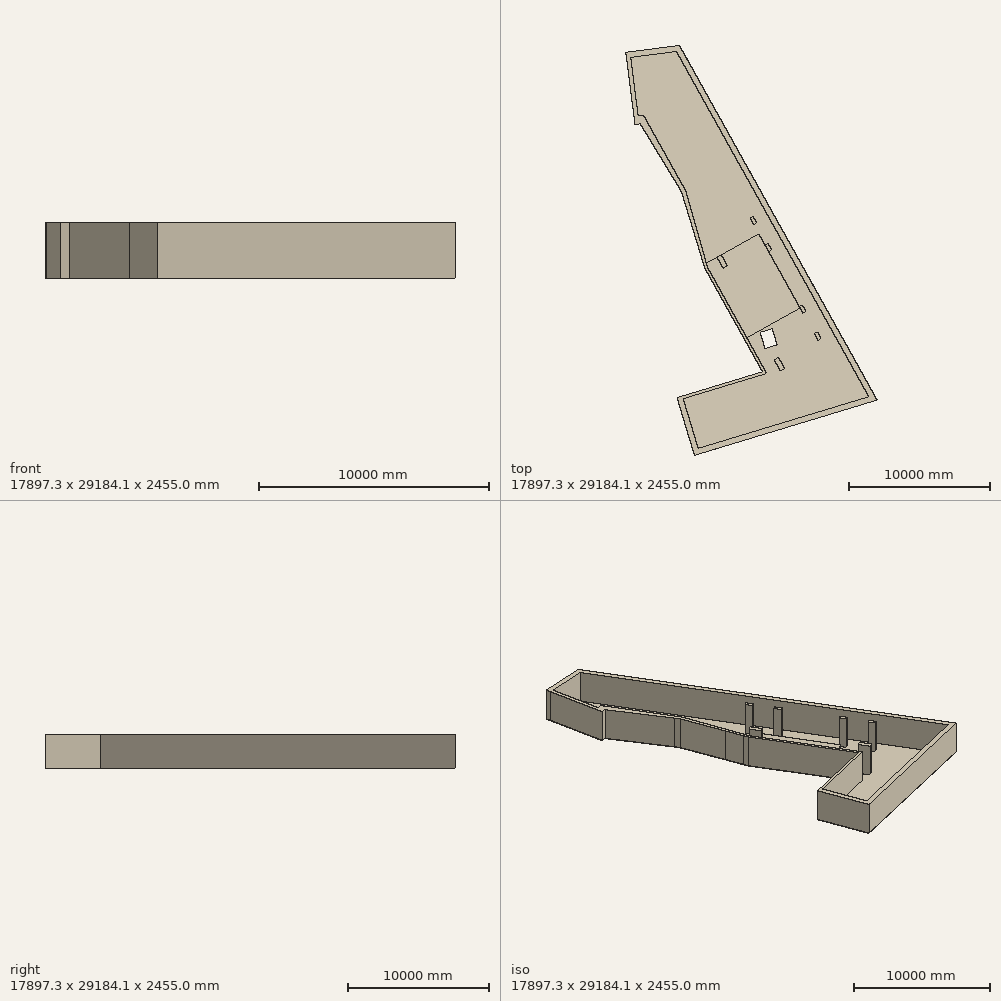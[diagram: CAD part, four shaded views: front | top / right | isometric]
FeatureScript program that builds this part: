
annotation { "Feature Type Name" : "Feature", "Feature Type Description" : "" }
export const myFeature = defineFeature(function(context is Context, id is Id, definition is map)
    precondition{}
    {
        {
            assignVariable(context, id + "F0", {"name" : "Ceiling", "anyValue" : 2430});
        }
        {
            var Q0;
            Q0=qCreatedBy(makeId("Top.planeOp"),FACE);
            var sketch = newSketch(context, id + "F1", { "sketchPlane" : qUnion([Q0])});
            skLineSegment(sketch, "E0", {"start": v(50356.24, 60225.68) * mm, "end": v(49220.2, 59881.82) * mm});
            skLineSegment(sketch, "E1", {"start": v(49220.2, 59881.82) * mm, "end": v(48658.24, 61738.46) * mm});
            skLineSegment(sketch, "E2", {"start": v(48658.24, 61738.46) * mm, "end": v(48436.53, 61671.35) * mm});
            skLineSegment(sketch, "E3", {"start": v(48436.53, 61671.35) * mm, "end": v(48364.1, 61910.63) * mm});
            skLineSegment(sketch, "E4", {"start": v(48364.1, 61910.63) * mm, "end": v(47885.55, 61765.78) * mm});
            skLineSegment(sketch, "E5", {"start": v(47885.55, 61765.78) * mm, "end": v(47957.97, 61526.5) * mm});
            skLineSegment(sketch, "E6", {"start": v(47957.97, 61526.5) * mm, "end": v(47686.86, 61444.44) * mm});
            skLineSegment(sketch, "E7", {"start": v(47686.86, 61444.44) * mm, "end": v(47759.29, 61205.16) * mm});
            skLineSegment(sketch, "E8", {"start": v(47759.29, 61205.16) * mm, "end": v(48491.38, 61426.75) * mm});
            skLineSegment(sketch, "E9", {"start": v(48491.38, 61426.75) * mm, "end": v(49070.78, 59512.52) * mm});
            skLineSegment(sketch, "E10", {"start": v(49070.78, 59512.52) * mm, "end": v(46721.47, 58801.43) * mm});
            skLineSegment(sketch, "E11", {"start": v(46721.47, 58801.43) * mm, "end": v(46142.07, 60715.66) * mm});
            skLineSegment(sketch, "E12", {"start": v(46142.07, 60715.66) * mm, "end": v(46706.46, 60886.5) * mm});
            skLineSegment(sketch, "E13", {"start": v(46706.46, 60886.5) * mm, "end": v(46634.03, 61125.77) * mm});
            skLineSegment(sketch, "E14", {"start": v(46634.03, 61125.77) * mm, "end": v(45451.68, 60767.9) * mm});
            skLineSegment(sketch, "E15", {"start": v(45451.68, 60767.9) * mm, "end": v(45524.1, 60528.62) * mm});
            skLineSegment(sketch, "E16", {"start": v(45524.1, 60528.62) * mm, "end": v(44643.85, 60262.18) * mm});
            skLineSegment(sketch, "E17", {"start": v(44643.85, 60262.18) * mm, "end": v(44571.42, 60501.46) * mm});
            skLineSegment(sketch, "E18", {"start": v(44571.42, 60501.46) * mm, "end": v(43824.87, 60275.5) * mm});
            skLineSegment(sketch, "E19", {"start": v(43824.87, 60275.5) * mm, "end": v(44386.83, 58418.88) * mm});
            skLineSegment(sketch, "E20", {"start": v(44386.83, 58418.88) * mm, "end": v(39132.43, 56828.48) * mm});
            skLineSegment(sketch, "E21", {"start": v(39132.43, 56828.48) * mm, "end": v(39132.43, 56828.48) * mm});
            skLineSegment(sketch, "E22", {"start": v(39132.43, 56828.48) * mm, "end": v(38458.91, 56624.62) * mm});
            skLineSegment(sketch, "E23", {"start": v(38458.91, 56624.62) * mm, "end": v(38574.8, 56241.77) * mm});
            skLineSegment(sketch, "E24", {"start": v(38574.8, 56241.77) * mm, "end": v(39350, 53680.63) * mm});
            skLineSegment(sketch, "E25", {"start": v(39350, 53680.63) * mm, "end": v(39348.17, 53681.01) * mm});
            skLineSegment(sketch, "E26", {"start": v(39348.17, 53681.01) * mm, "end": v(39517.02, 53123.18) * mm});
            skLineSegment(sketch, "E27", {"start": v(39517.02, 53123.18) * mm, "end": v(36984.61, 52356.67) * mm});
            skLineSegment(sketch, "E28", {"start": v(36984.61, 52356.67) * mm, "end": v(36288.15, 54657.64) * mm});
            skLineSegment(sketch, "E29", {"start": v(36288.15, 54657.64) * mm, "end": v(36288.98, 54657.9) * mm});
            skLineSegment(sketch, "E30", {"start": v(36288.98, 54657.9) * mm, "end": v(35925.26, 55857.73) * mm});
            skLineSegment(sketch, "E31", {"start": v(35925.26, 55857.73) * mm, "end": v(30957.21, 72270.12) * mm});
            skLineSegment(sketch, "E32", {"start": v(30957.21, 72270.12) * mm, "end": v(52856.55, 75078.33) * mm});
            skLineSegment(sketch, "E33", {"start": v(52856.55, 75078.33) * mm, "end": v(64538.41, 54127.57) * mm});
            skLineSegment(sketch, "E34", {"start": v(64538.41, 54127.57) * mm, "end": v(66559.72, 50502.1) * mm});
            skLineSegment(sketch, "E35", {"start": v(66559.72, 50502.1) * mm, "end": v(54412.26, 46825.31) * mm});
            skLineSegment(sketch, "E36", {"start": v(54412.26, 46825.31) * mm, "end": v(53342.81, 50358.57) * mm});
            skLineSegment(sketch, "E37", {"start": v(53342.81, 50358.57) * mm, "end": v(59288.18, 52158.11) * mm});
            skLineSegment(sketch, "E38", {"start": v(59288.18, 52158.11) * mm, "end": v(59106.76, 52483.52) * mm});
            skLineSegment(sketch, "E39", {"start": v(59106.76, 52483.52) * mm, "end": v(55867.2, 58292.84) * mm});
            skLineSegment(sketch, "E40", {"start": v(55867.2, 58292.84) * mm, "end": v(51354.69, 56926.99) * mm});
            skLineSegment(sketch, "E41", {"start": v(51354.69, 56926.99) * mm, "end": v(50356.24, 60225.68) * mm});
            skCircle(sketch, "E42", {"center": v(0, 0) * mm, "radius": 1927.6 * mm});
            skLineSegment(sketch, "E43", {"start": v(0, 5000) * mm, "end": v(0, -5000) * mm});
            skLineSegment(sketch, "E44", {"start": v(5000, 0) * mm, "end": v(-5000, 0) * mm});
            skLineSegment(sketch, "E45", {"start": v(52857.63, 75079.51) * mm, "end": v(52856.55, 75078.33) * mm});
            skLineSegment(sketch, "E46", {"start": v(52856.55, 75078.33) * mm, "end": v(56743.09, 68109.43) * mm});
            skLineSegment(sketch, "E47", {"start": v(56743.09, 68109.43) * mm, "end": v(52142.28, 67923.68) * mm});
            skLineSegment(sketch, "E48", {"start": v(52142.28, 67923.68) * mm, "end": v(32512.63, 67131.17) * mm});
            skLineSegment(sketch, "E49", {"start": v(32512.63, 67131.17) * mm, "end": v(32512.63, 67131.18) * mm});
            skLineSegment(sketch, "E50", {"start": v(32512.63, 67131.18) * mm, "end": v(30957.18, 72270.11) * mm});
            skLineSegment(sketch, "E51", {"start": v(30957.18, 72270.11) * mm, "end": v(49304.34, 74623.7) * mm});
            skLineSegment(sketch, "E52", {"start": v(49304.34, 74623.7) * mm, "end": v(49304.34, 74623.69) * mm});
            skLineSegment(sketch, "E53", {"start": v(49304.34, 74623.69) * mm, "end": v(51228.96, 74870.57) * mm});
            skLineSegment(sketch, "E54", {"start": v(51228.96, 74870.57) * mm, "end": v(52856, 75079.3) * mm});
            skLineSegment(sketch, "E55", {"start": v(44184.43, 60123.13) * mm, "end": v(45964.6, 60661.95) * mm});
            skLineSegment(sketch, "E56", {"start": v(45964.6, 60661.95) * mm, "end": v(46549.88, 58728.5) * mm});
            skLineSegment(sketch, "E57", {"start": v(46549.88, 58728.5) * mm, "end": v(44769.56, 58189.64) * mm});
            skLineSegment(sketch, "E58", {"start": v(44769.56, 58189.64) * mm, "end": v(44184.43, 60123.12) * mm});
            skLineSegment(sketch, "E59", {"start": v(44184.43, 60123.12) * mm, "end": v(44184.43, 60123.13) * mm});
            skLineSegment(sketch, "E60", {"start": v(35925.26, 55857.73) * mm, "end": v(32512.63, 67131.18) * mm});
            skLineSegment(sketch, "E61", {"start": v(32512.63, 67131.18) * mm, "end": v(56743.09, 68109.43) * mm});
            skLineSegment(sketch, "E62", {"start": v(56743.09, 68109.43) * mm, "end": v(64538.41, 54127.57) * mm});
            skLineSegment(sketch, "E63", {"start": v(53342.81, 50358.57) * mm, "end": v(51750.13, 55620.52) * mm});
            skLineSegment(sketch, "E64", {"start": v(51750.13, 55620.52) * mm, "end": v(52375.23, 55809.73) * mm});
            skLineSegment(sketch, "E65", {"start": v(52375.23, 55809.73) * mm, "end": v(53909.98, 50739.2) * mm});
            skLineSegment(sketch, "E66", {"start": v(53909.98, 50739.2) * mm, "end": v(57604, 51858.9) * mm});
            skLineSegment(sketch, "E67", {"start": v(57604, 51858.9) * mm, "end": v(55674.23, 58234.43) * mm});
            skLineSegment(sketch, "E68", {"start": v(55674.23, 58234.43) * mm, "end": v(51354.69, 56926.99) * mm});
            skLineSegment(sketch, "E69", {"start": v(51354.69, 56926.99) * mm, "end": v(55674.23, 58234.43) * mm});
            skLineSegment(sketch, "E70", {"start": v(55674.23, 58234.43) * mm, "end": v(57604.42, 51857.43) * mm});
            skLineSegment(sketch, "E71", {"start": v(57604.42, 51857.43) * mm, "end": v(53909.98, 50739.2) * mm});
            skLineSegment(sketch, "E72", {"start": v(53909.98, 50739.2) * mm, "end": v(52375.23, 55809.73) * mm});
            skLineSegment(sketch, "E73", {"start": v(52375.23, 55809.73) * mm, "end": v(51750.13, 55620.52) * mm});
            skLineSegment(sketch, "E74", {"start": v(51750.13, 55620.52) * mm, "end": v(51354.69, 56926.99) * mm});
            skLineSegment(sketch, "E75", {"start": v(43785.9, 47980.97) * mm, "end": v(41725.14, 54896.4) * mm});
            skLineSegment(sketch, "E76", {"start": v(41725.14, 54896.4) * mm, "end": v(48582.16, 57001.67) * mm});
            skLineSegment(sketch, "E77", {"start": v(48582.16, 57001.67) * mm, "end": v(50679.83, 50071.15) * mm});
            skLineSegment(sketch, "E78", {"start": v(50679.83, 50071.15) * mm, "end": v(47628.14, 49145.9) * mm});
            skLineSegment(sketch, "E79", {"start": v(47628.14, 49145.9) * mm, "end": v(47641.24, 49102.68) * mm});
            skLineSegment(sketch, "E80", {"start": v(47641.24, 49102.68) * mm, "end": v(46838.37, 48859.26) * mm});
            skLineSegment(sketch, "E81", {"start": v(46838.37, 48859.26) * mm, "end": v(46825.27, 48902.48) * mm});
            skLineSegment(sketch, "E82", {"start": v(46825.27, 48902.48) * mm, "end": v(43785.9, 47980.97) * mm});
            skLineSegment(sketch, "E83", {"start": v(43985.95, 48355.1) * mm, "end": v(50305.83, 50271.24) * mm});
            skLineSegment(sketch, "E84", {"start": v(43784.47, 47980.54) * mm, "end": v(50679.83, 50071.15) * mm});
            skLineSegment(sketch, "E85", {"start": v(42097.56, 54696.9) * mm, "end": v(43985.95, 48355.1) * mm});
            skLineSegment(sketch, "E86", {"start": v(41725.14, 54896.4) * mm, "end": v(43784.47, 47980.54) * mm});
            skLineSegment(sketch, "E87", {"start": v(48382.3, 56626.46) * mm, "end": v(42097.56, 54696.9) * mm});
            skLineSegment(sketch, "E88", {"start": v(48582.17, 57001.65) * mm, "end": v(41725.14, 54896.4) * mm});
            skLineSegment(sketch, "E89", {"start": v(50305.83, 50271.24) * mm, "end": v(48382.3, 56626.46) * mm});
            skLineSegment(sketch, "E90", {"start": v(50679.83, 50071.15) * mm, "end": v(48582.17, 57001.65) * mm});
            skLineSegment(sketch, "E91", {"start": v(57792.28, 52268.48) * mm, "end": v(58968.18, 52624.48) * mm});
            skLineSegment(sketch, "E92", {"start": v(59098.58, 52193.79) * mm, "end": v(58968.18, 52624.48) * mm});
            skLineSegment(sketch, "E93", {"start": v(57922.67, 51837.79) * mm, "end": v(59098.58, 52193.79) * mm});
            skLineSegment(sketch, "E94", {"start": v(57922.67, 51837.79) * mm, "end": v(57792.28, 52268.48) * mm});
            skLineSegment(sketch, "E95", {"start": v(61899.36, 49097.97) * mm, "end": v(50281.68, 69933.64) * mm});
            skLineSegment(sketch, "E96", {"start": v(55070.83, 59721.1) * mm, "end": v(59287.5, 52158.7) * mm});
            skLineSegment(sketch, "E97", {"start": v(54896.15, 59623.7) * mm, "end": v(58991.9, 52278.2) * mm});
            skLineSegment(sketch, "E98", {"start": v(55911.81, 59846.47) * mm, "end": v(50927.73, 58337.56) * mm});
            skLineSegment(sketch, "E99", {"start": v(51575.28, 74914.98) * mm, "end": v(49601.81, 74661.66) * mm});
            skLineSegment(sketch, "E100", {"start": v(49601.81, 74661.66) * mm, "end": v(50012.55, 71444.1) * mm});
            skLineSegment(sketch, "E101", {"start": v(50012.55, 71444.1) * mm, "end": v(62198.73, 49586.37) * mm});
            skLineSegment(sketch, "E102", {"start": v(62198.73, 49586.37) * mm, "end": v(64867.16, 51074.04) * mm});
            skLineSegment(sketch, "E103", {"start": v(64867.16, 51074.04) * mm, "end": v(51575.28, 74914.98) * mm});
            skLineSegment(sketch, "E104", {"start": v(51980.16, 57115.1) * mm, "end": v(55674.65, 58233.32) * mm});
            skLineSegment(sketch, "E105", {"start": v(55674.65, 58233.32) * mm, "end": v(57604, 51858.9) * mm});
            skLineSegment(sketch, "E106", {"start": v(57604, 51858.9) * mm, "end": v(53909.52, 50740.69) * mm});
            skLineSegment(sketch, "E107", {"start": v(53909.52, 50740.69) * mm, "end": v(51980.16, 57115.1) * mm});
            skLineSegment(sketch, "E108", {"start": v(55694.63, 56724.4) * mm, "end": v(55675.8, 56786.62) * mm});
            skLineSegment(sketch, "E109", {"start": v(55675.8, 56786.62) * mm, "end": v(55672.2, 56785.53) * mm});
            skArc(sketch, "E110", {"start": v(55672.2, 56785.53) * mm, "mid": v(55669.63, 56783.5) * mm, "end": v(55669.12, 56780.27) * mm});
            skLineSegment(sketch, "E111", {"start": v(55669.12, 56780.27) * mm, "end": v(55678.43, 56737.44) * mm});
            skArc(sketch, "E112", {"start": v(55671.21, 56725.15) * mm, "mid": v(55677.22, 56729.88) * mm, "end": v(55678.43, 56737.44) * mm});
            skLineSegment(sketch, "E113", {"start": v(55671.21, 56725.15) * mm, "end": v(55560.55, 56691.66) * mm});
            skArc(sketch, "E114", {"start": v(55547.74, 56697.88) * mm, "mid": v(55552.93, 56692.26) * mm, "end": v(55560.55, 56691.66) * mm});
            skLineSegment(sketch, "E115", {"start": v(55547.74, 56697.88) * mm, "end": v(55531.74, 56738.69) * mm});
            skArc(sketch, "E116", {"start": v(55531.74, 56738.69) * mm, "mid": v(55529.51, 56741.1) * mm, "end": v(55526.24, 56741.35) * mm});
            skLineSegment(sketch, "E117", {"start": v(55526.24, 56741.35) * mm, "end": v(55522.66, 56740.27) * mm});
            skLineSegment(sketch, "E118", {"start": v(55522.66, 56740.27) * mm, "end": v(55541.49, 56678.05) * mm});
            skLineSegment(sketch, "E119", {"start": v(55541.49, 56678.05) * mm, "end": v(55694.63, 56724.4) * mm});
            skLineSegment(sketch, "E120", {"start": v(55616.8, 56429.2) * mm, "end": v(55635.64, 56366.99) * mm});
            skLineSegment(sketch, "E121", {"start": v(55635.64, 56366.99) * mm, "end": v(55639.22, 56368.08) * mm});
            skArc(sketch, "E122", {"start": v(55639.22, 56368.08) * mm, "mid": v(55641.8, 56370.1) * mm, "end": v(55642.32, 56373.34) * mm});
            skLineSegment(sketch, "E123", {"start": v(55642.32, 56373.34) * mm, "end": v(55633, 56416.17) * mm});
            skArc(sketch, "E124", {"start": v(55640.22, 56428.45) * mm, "mid": v(55634.2, 56423.72) * mm, "end": v(55633, 56416.17) * mm});
            skLineSegment(sketch, "E125", {"start": v(55640.22, 56428.45) * mm, "end": v(55750.88, 56461.95) * mm});
            skArc(sketch, "E126", {"start": v(55763.7, 56455.73) * mm, "mid": v(55758.5, 56461.34) * mm, "end": v(55750.88, 56461.95) * mm});
            skLineSegment(sketch, "E127", {"start": v(55763.7, 56455.73) * mm, "end": v(55779.7, 56414.92) * mm});
            skArc(sketch, "E128", {"start": v(55779.7, 56414.92) * mm, "mid": v(55781.92, 56412.51) * mm, "end": v(55785.19, 56412.26) * mm});
            skLineSegment(sketch, "E129", {"start": v(55785.19, 56412.26) * mm, "end": v(55788.78, 56413.34) * mm});
            skLineSegment(sketch, "E130", {"start": v(55788.78, 56413.34) * mm, "end": v(55769.95, 56475.55) * mm});
            skLineSegment(sketch, "E131", {"start": v(55769.95, 56475.55) * mm, "end": v(55616.8, 56429.2) * mm});
            skCircle(sketch, "E132", {"center": v(55655.72, 56576.8) * mm, "radius": 0.25 * mm});
            skCircle(sketch, "E133", {"center": v(55733.93, 56318.38) * mm, "radius": 9 * mm});
            skCircle(sketch, "E134", {"center": v(55577.5, 56835.23) * mm, "radius": 9 * mm});
            skCircle(sketch, "E135", {"center": v(55405.22, 56783.08) * mm, "radius": 9 * mm});
            skCircle(sketch, "E136", {"center": v(55561.65, 56266.24) * mm, "radius": 9 * mm});
            skLineSegment(sketch, "E137", {"start": v(55367.81, 56803.1) * mm, "end": v(55654.95, 56890.01) * mm});
            skLineSegment(sketch, "E138", {"start": v(55541.63, 56228.83) * mm, "end": v(55367.81, 56803.1) * mm});
            skLineSegment(sketch, "E139", {"start": v(55828.76, 56315.74) * mm, "end": v(55541.63, 56228.83) * mm});
            skLineSegment(sketch, "E140", {"start": v(55654.95, 56890.01) * mm, "end": v(55828.76, 56315.74) * mm});
            skCircle(sketch, "E141", {"center": v(55655.72, 56576.8) * mm, "radius": 57.5 * mm});
            skCircle(sketch, "E142", {"center": v(55655.72, 56576.8) * mm, "radius": 59.5 * mm});
            skCircle(sketch, "E143", {"center": v(55655.72, 56576.8) * mm, "radius": 63.5 * mm});
            skLineSegment(sketch, "E144", {"start": v(55607.5, 56356.38) * mm, "end": v(55636.22, 56365.08) * mm});
            skLineSegment(sketch, "E145", {"start": v(55636.22, 56365.08) * mm, "end": v(55621.73, 56412.93) * mm});
            skLineSegment(sketch, "E146", {"start": v(55621.73, 56412.93) * mm, "end": v(55593.02, 56404.24) * mm});
            skLineSegment(sketch, "E147", {"start": v(55593.02, 56404.24) * mm, "end": v(55607.5, 56356.38) * mm});
            skLineSegment(sketch, "E148", {"start": v(55636.22, 56365.08) * mm, "end": v(55635.64, 56366.99) * mm});
            skLineSegment(sketch, "E149", {"start": v(55635.64, 56366.99) * mm, "end": v(55621.73, 56412.93) * mm});
            skLineSegment(sketch, "E150", {"start": v(52875.62, 55599.52) * mm, "end": v(52894.45, 55537.3) * mm});
            skLineSegment(sketch, "E151", {"start": v(52894.45, 55537.3) * mm, "end": v(52898.03, 55538.4) * mm});
            skArc(sketch, "E152", {"start": v(52898.03, 55538.4) * mm, "mid": v(52900.6, 55540.42) * mm, "end": v(52901.13, 55543.66) * mm});
            skLineSegment(sketch, "E153", {"start": v(52901.13, 55543.66) * mm, "end": v(52891.81, 55586.5) * mm});
            skArc(sketch, "E154", {"start": v(52899.03, 55598.77) * mm, "mid": v(52893.02, 55594.04) * mm, "end": v(52891.81, 55586.5) * mm});
            skLineSegment(sketch, "E155", {"start": v(52899.03, 55598.77) * mm, "end": v(53009.69, 55632.26) * mm});
            skArc(sketch, "E156", {"start": v(53022.5, 55626.05) * mm, "mid": v(53017.31, 55631.66) * mm, "end": v(53009.69, 55632.26) * mm});
            skLineSegment(sketch, "E157", {"start": v(53022.5, 55626.05) * mm, "end": v(53038.5, 55585.24) * mm});
            skArc(sketch, "E158", {"start": v(53038.5, 55585.24) * mm, "mid": v(53040.73, 55582.83) * mm, "end": v(53044, 55582.57) * mm});
            skLineSegment(sketch, "E159", {"start": v(53044, 55582.57) * mm, "end": v(53047.59, 55583.66) * mm});
            skLineSegment(sketch, "E160", {"start": v(53047.59, 55583.66) * mm, "end": v(53028.76, 55645.87) * mm});
            skLineSegment(sketch, "E161", {"start": v(53028.76, 55645.87) * mm, "end": v(52875.62, 55599.52) * mm});
            skLineSegment(sketch, "E162", {"start": v(52953.44, 55894.72) * mm, "end": v(52934.6, 55956.94) * mm});
            skLineSegment(sketch, "E163", {"start": v(52934.6, 55956.94) * mm, "end": v(52931.02, 55955.85) * mm});
            skArc(sketch, "E164", {"start": v(52931.02, 55955.85) * mm, "mid": v(52928.44, 55953.82) * mm, "end": v(52927.92, 55950.59) * mm});
            skLineSegment(sketch, "E165", {"start": v(52927.92, 55950.59) * mm, "end": v(52937.24, 55907.75) * mm});
            skArc(sketch, "E166", {"start": v(52930.02, 55895.47) * mm, "mid": v(52936.03, 55900.2) * mm, "end": v(52937.24, 55907.75) * mm});
            skLineSegment(sketch, "E167", {"start": v(52930.02, 55895.47) * mm, "end": v(52819.36, 55861.98) * mm});
            skArc(sketch, "E168", {"start": v(52806.55, 55868.2) * mm, "mid": v(52811.74, 55862.58) * mm, "end": v(52819.36, 55861.98) * mm});
            skLineSegment(sketch, "E169", {"start": v(52806.55, 55868.2) * mm, "end": v(52790.55, 55909) * mm});
            skArc(sketch, "E170", {"start": v(52790.55, 55909) * mm, "mid": v(52788.32, 55911.41) * mm, "end": v(52785.05, 55911.67) * mm});
            skLineSegment(sketch, "E171", {"start": v(52785.05, 55911.67) * mm, "end": v(52781.47, 55910.59) * mm});
            skLineSegment(sketch, "E172", {"start": v(52781.47, 55910.59) * mm, "end": v(52800.3, 55848.37) * mm});
            skLineSegment(sketch, "E173", {"start": v(52800.3, 55848.37) * mm, "end": v(52953.44, 55894.72) * mm});
            skCircle(sketch, "E174", {"center": v(52914.53, 55747.12) * mm, "radius": 0.25 * mm});
            skCircle(sketch, "E175", {"center": v(52836.3, 56005.54) * mm, "radius": 9 * mm});
            skCircle(sketch, "E176", {"center": v(52992.74, 55488.7) * mm, "radius": 9 * mm});
            skCircle(sketch, "E177", {"center": v(53165.02, 55540.84) * mm, "radius": 9 * mm});
            skCircle(sketch, "E178", {"center": v(53008.6, 56057.69) * mm, "radius": 9 * mm});
            skLineSegment(sketch, "E179", {"start": v(53202.43, 55520.82) * mm, "end": v(52915.3, 55433.91) * mm});
            skLineSegment(sketch, "E180", {"start": v(53028.61, 56095.1) * mm, "end": v(53202.43, 55520.82) * mm});
            skLineSegment(sketch, "E181", {"start": v(52741.48, 56008.19) * mm, "end": v(53028.61, 56095.1) * mm});
            skLineSegment(sketch, "E182", {"start": v(52915.3, 55433.91) * mm, "end": v(52741.48, 56008.19) * mm});
            skCircle(sketch, "E183", {"center": v(52914.53, 55747.12) * mm, "radius": 57.5 * mm});
            skCircle(sketch, "E184", {"center": v(52914.53, 55747.12) * mm, "radius": 59.5 * mm});
            skCircle(sketch, "E185", {"center": v(52914.53, 55747.12) * mm, "radius": 63.5 * mm});
            skLineSegment(sketch, "E186", {"start": v(53045.04, 55592.08) * mm, "end": v(53073.75, 55600.77) * mm});
            skLineSegment(sketch, "E187", {"start": v(53073.75, 55600.77) * mm, "end": v(53062.4, 55638.3) * mm});
            skLineSegment(sketch, "E188", {"start": v(53062.4, 55638.3) * mm, "end": v(53033.68, 55629.6) * mm});
            skLineSegment(sketch, "E189", {"start": v(53033.68, 55629.6) * mm, "end": v(53045.04, 55592.08) * mm});
            skLineSegment(sketch, "E190", {"start": v(53076.88, 55590.44) * mm, "end": v(53073.75, 55600.77) * mm});
            skLineSegment(sketch, "E191", {"start": v(53048.16, 55581.75) * mm, "end": v(53076.88, 55590.44) * mm});
            skLineSegment(sketch, "E192", {"start": v(53048.16, 55581.75) * mm, "end": v(53047.59, 55583.66) * mm});
            skLineSegment(sketch, "E193", {"start": v(53602.75, 53197.13) * mm, "end": v(53621.58, 53134.91) * mm});
            skLineSegment(sketch, "E194", {"start": v(53621.58, 53134.91) * mm, "end": v(53625.16, 53136) * mm});
            skArc(sketch, "E195", {"start": v(53625.16, 53136) * mm, "mid": v(53627.74, 53138.03) * mm, "end": v(53628.26, 53141.26) * mm});
            skLineSegment(sketch, "E196", {"start": v(53628.26, 53141.26) * mm, "end": v(53618.94, 53184.1) * mm});
            skArc(sketch, "E197", {"start": v(53626.16, 53196.38) * mm, "mid": v(53620.15, 53191.65) * mm, "end": v(53618.94, 53184.1) * mm});
            skLineSegment(sketch, "E198", {"start": v(53626.16, 53196.38) * mm, "end": v(53736.82, 53229.87) * mm});
            skArc(sketch, "E199", {"start": v(53749.63, 53223.65) * mm, "mid": v(53744.44, 53229.27) * mm, "end": v(53736.82, 53229.87) * mm});
            skLineSegment(sketch, "E200", {"start": v(53749.63, 53223.65) * mm, "end": v(53765.64, 53182.84) * mm});
            skArc(sketch, "E201", {"start": v(53765.64, 53182.84) * mm, "mid": v(53767.86, 53180.44) * mm, "end": v(53771.13, 53180.18) * mm});
            skLineSegment(sketch, "E202", {"start": v(53771.13, 53180.18) * mm, "end": v(53774.72, 53181.26) * mm});
            skLineSegment(sketch, "E203", {"start": v(53774.72, 53181.26) * mm, "end": v(53755.89, 53243.48) * mm});
            skLineSegment(sketch, "E204", {"start": v(53755.89, 53243.48) * mm, "end": v(53602.75, 53197.13) * mm});
            skLineSegment(sketch, "E205", {"start": v(53680.56, 53492.33) * mm, "end": v(53661.73, 53554.54) * mm});
            skLineSegment(sketch, "E206", {"start": v(53661.73, 53554.54) * mm, "end": v(53658.15, 53553.46) * mm});
            skArc(sketch, "E207", {"start": v(53658.15, 53553.46) * mm, "mid": v(53655.57, 53551.43) * mm, "end": v(53655.05, 53548.2) * mm});
            skLineSegment(sketch, "E208", {"start": v(53655.05, 53548.2) * mm, "end": v(53664.37, 53505.36) * mm});
            skArc(sketch, "E209", {"start": v(53657.15, 53493.08) * mm, "mid": v(53663.16, 53497.8) * mm, "end": v(53664.37, 53505.36) * mm});
            skLineSegment(sketch, "E210", {"start": v(53657.15, 53493.08) * mm, "end": v(53546.5, 53459.59) * mm});
            skArc(sketch, "E211", {"start": v(53533.68, 53465.8) * mm, "mid": v(53538.87, 53460.19) * mm, "end": v(53546.5, 53459.59) * mm});
            skLineSegment(sketch, "E212", {"start": v(53533.68, 53465.8) * mm, "end": v(53517.68, 53506.61) * mm});
            skArc(sketch, "E213", {"start": v(53517.68, 53506.61) * mm, "mid": v(53515.45, 53509.02) * mm, "end": v(53512.18, 53509.28) * mm});
            skLineSegment(sketch, "E214", {"start": v(53512.18, 53509.28) * mm, "end": v(53508.6, 53508.2) * mm});
            skLineSegment(sketch, "E215", {"start": v(53508.6, 53508.2) * mm, "end": v(53527.43, 53445.98) * mm});
            skLineSegment(sketch, "E216", {"start": v(53527.43, 53445.98) * mm, "end": v(53680.56, 53492.33) * mm});
            skCircle(sketch, "E217", {"center": v(53641.66, 53344.73) * mm, "radius": 0.25 * mm});
            skCircle(sketch, "E218", {"center": v(53563.44, 53603.15) * mm, "radius": 9 * mm});
            skCircle(sketch, "E219", {"center": v(53719.87, 53086.3) * mm, "radius": 9 * mm});
            skCircle(sketch, "E220", {"center": v(53892.15, 53138.45) * mm, "radius": 9 * mm});
            skCircle(sketch, "E221", {"center": v(53735.72, 53655.3) * mm, "radius": 9 * mm});
            skLineSegment(sketch, "E222", {"start": v(53929.56, 53118.43) * mm, "end": v(53642.42, 53031.52) * mm});
            skLineSegment(sketch, "E223", {"start": v(53755.74, 53692.7) * mm, "end": v(53929.56, 53118.43) * mm});
            skLineSegment(sketch, "E224", {"start": v(53468.6, 53605.8) * mm, "end": v(53755.74, 53692.7) * mm});
            skLineSegment(sketch, "E225", {"start": v(53642.42, 53031.52) * mm, "end": v(53468.6, 53605.8) * mm});
            skCircle(sketch, "E226", {"center": v(53641.66, 53344.73) * mm, "radius": 57.5 * mm});
            skCircle(sketch, "E227", {"center": v(53641.66, 53344.73) * mm, "radius": 59.5 * mm});
            skCircle(sketch, "E228", {"center": v(53641.66, 53344.73) * mm, "radius": 63.5 * mm});
            skLineSegment(sketch, "E229", {"start": v(53689.87, 53565.15) * mm, "end": v(53661.16, 53556.46) * mm});
            skLineSegment(sketch, "E230", {"start": v(53661.16, 53556.46) * mm, "end": v(53675.64, 53508.6) * mm});
            skLineSegment(sketch, "E231", {"start": v(53675.64, 53508.6) * mm, "end": v(53704.35, 53517.3) * mm});
            skLineSegment(sketch, "E232", {"start": v(53704.35, 53517.3) * mm, "end": v(53689.87, 53565.15) * mm});
            skLineSegment(sketch, "E233", {"start": v(53661.16, 53556.46) * mm, "end": v(53661.73, 53554.54) * mm});
            skLineSegment(sketch, "E234", {"start": v(53661.73, 53554.54) * mm, "end": v(53675.64, 53508.6) * mm});
            skLineSegment(sketch, "E235", {"start": v(56421.76, 54322) * mm, "end": v(56402.93, 54384.22) * mm});
            skLineSegment(sketch, "E236", {"start": v(56402.93, 54384.22) * mm, "end": v(56399.34, 54383.14) * mm});
            skArc(sketch, "E237", {"start": v(56399.34, 54383.14) * mm, "mid": v(56396.76, 54381.1) * mm, "end": v(56396.24, 54377.87) * mm});
            skLineSegment(sketch, "E238", {"start": v(56396.24, 54377.87) * mm, "end": v(56405.56, 54335.04) * mm});
            skArc(sketch, "E239", {"start": v(56398.34, 54322.76) * mm, "mid": v(56404.35, 54327.49) * mm, "end": v(56405.56, 54335.04) * mm});
            skLineSegment(sketch, "E240", {"start": v(56398.34, 54322.76) * mm, "end": v(56287.68, 54289.27) * mm});
            skArc(sketch, "E241", {"start": v(56274.87, 54295.48) * mm, "mid": v(56280.06, 54289.87) * mm, "end": v(56287.68, 54289.27) * mm});
            skLineSegment(sketch, "E242", {"start": v(56274.87, 54295.48) * mm, "end": v(56258.87, 54336.3) * mm});
            skArc(sketch, "E243", {"start": v(56258.87, 54336.3) * mm, "mid": v(56256.64, 54338.7) * mm, "end": v(56253.37, 54338.96) * mm});
            skLineSegment(sketch, "E244", {"start": v(56253.37, 54338.96) * mm, "end": v(56249.79, 54337.87) * mm});
            skLineSegment(sketch, "E245", {"start": v(56249.79, 54337.87) * mm, "end": v(56268.62, 54275.66) * mm});
            skLineSegment(sketch, "E246", {"start": v(56268.62, 54275.66) * mm, "end": v(56421.76, 54322) * mm});
            skLineSegment(sketch, "E247", {"start": v(56343.94, 54026.8) * mm, "end": v(56362.77, 53964.6) * mm});
            skLineSegment(sketch, "E248", {"start": v(56362.77, 53964.6) * mm, "end": v(56366.35, 53965.68) * mm});
            skArc(sketch, "E249", {"start": v(56366.35, 53965.68) * mm, "mid": v(56368.93, 53967.7) * mm, "end": v(56369.45, 53970.94) * mm});
            skLineSegment(sketch, "E250", {"start": v(56369.45, 53970.94) * mm, "end": v(56360.13, 54013.78) * mm});
            skArc(sketch, "E251", {"start": v(56367.35, 54026.06) * mm, "mid": v(56361.34, 54021.33) * mm, "end": v(56360.13, 54013.78) * mm});
            skLineSegment(sketch, "E252", {"start": v(56367.35, 54026.06) * mm, "end": v(56478, 54059.55) * mm});
            skArc(sketch, "E253", {"start": v(56490.82, 54053.33) * mm, "mid": v(56485.63, 54058.95) * mm, "end": v(56478, 54059.55) * mm});
            skLineSegment(sketch, "E254", {"start": v(56490.82, 54053.33) * mm, "end": v(56506.83, 54012.52) * mm});
            skArc(sketch, "E255", {"start": v(56506.83, 54012.52) * mm, "mid": v(56509.05, 54010.12) * mm, "end": v(56512.32, 54009.86) * mm});
            skLineSegment(sketch, "E256", {"start": v(56512.32, 54009.86) * mm, "end": v(56515.9, 54010.95) * mm});
            skLineSegment(sketch, "E257", {"start": v(56515.9, 54010.95) * mm, "end": v(56497.08, 54073.16) * mm});
            skLineSegment(sketch, "E258", {"start": v(56497.08, 54073.16) * mm, "end": v(56343.94, 54026.8) * mm});
            skCircle(sketch, "E259", {"center": v(56382.85, 54174.4) * mm, "radius": 0.25 * mm});
            skCircle(sketch, "E260", {"center": v(56461.06, 53915.99) * mm, "radius": 9 * mm});
            skCircle(sketch, "E261", {"center": v(56304.63, 54432.83) * mm, "radius": 9 * mm});
            skCircle(sketch, "E262", {"center": v(56132.35, 54380.69) * mm, "radius": 9 * mm});
            skCircle(sketch, "E263", {"center": v(56288.78, 53863.84) * mm, "radius": 9 * mm});
            skLineSegment(sketch, "E264", {"start": v(56094.94, 54400.7) * mm, "end": v(56382.08, 54487.62) * mm});
            skLineSegment(sketch, "E265", {"start": v(56268.76, 53826.44) * mm, "end": v(56094.94, 54400.7) * mm});
            skLineSegment(sketch, "E266", {"start": v(56555.9, 53913.35) * mm, "end": v(56268.76, 53826.44) * mm});
            skLineSegment(sketch, "E267", {"start": v(56382.08, 54487.62) * mm, "end": v(56555.9, 53913.35) * mm});
            skCircle(sketch, "E268", {"center": v(56382.85, 54174.4) * mm, "radius": 57.5 * mm});
            skCircle(sketch, "E269", {"center": v(56382.85, 54174.4) * mm, "radius": 59.5 * mm});
            skCircle(sketch, "E270", {"center": v(56382.85, 54174.4) * mm, "radius": 63.5 * mm});
            skLineSegment(sketch, "E271", {"start": v(56252.34, 54329.45) * mm, "end": v(56223.62, 54320.76) * mm});
            skLineSegment(sketch, "E272", {"start": v(56223.62, 54320.76) * mm, "end": v(56234.98, 54283.24) * mm});
            skLineSegment(sketch, "E273", {"start": v(56234.98, 54283.24) * mm, "end": v(56263.7, 54291.93) * mm});
            skLineSegment(sketch, "E274", {"start": v(56263.7, 54291.93) * mm, "end": v(56252.34, 54329.45) * mm});
            skLineSegment(sketch, "E275", {"start": v(56220.5, 54331.1) * mm, "end": v(56223.62, 54320.76) * mm});
            skLineSegment(sketch, "E276", {"start": v(56249.2, 54339.79) * mm, "end": v(56220.5, 54331.1) * mm});
            skLineSegment(sketch, "E277", {"start": v(56249.2, 54339.79) * mm, "end": v(56249.79, 54337.87) * mm});
            skLineSegment(sketch, "E278", {"start": v(57251.35, 51929.78) * mm, "end": v(57238.9, 51926.01) * mm});
            skLineSegment(sketch, "E279", {"start": v(57238.9, 51926.01) * mm, "end": v(57192.55, 52079.15) * mm});
            skLineSegment(sketch, "E280", {"start": v(57192.55, 52079.15) * mm, "end": v(57205, 52082.92) * mm});
            skLineSegment(sketch, "E281", {"start": v(57205, 52082.92) * mm, "end": v(57222.67, 52024.54) * mm});
            skArc(sketch, "E282", {"start": v(57222.67, 52024.54) * mm, "mid": v(57229.95, 52015.66) * mm, "end": v(57241.37, 52014.52) * mm});
            skLineSegment(sketch, "E283", {"start": v(57241.37, 52014.52) * mm, "end": v(57340.91, 52044.65) * mm});
            skArc(sketch, "E284", {"start": v(57340.91, 52044.65) * mm, "mid": v(57349.8, 52051.93) * mm, "end": v(57350.92, 52063.35) * mm});
            skLineSegment(sketch, "E285", {"start": v(57350.92, 52063.35) * mm, "end": v(57333.25, 52121.74) * mm});
            skLineSegment(sketch, "E286", {"start": v(57333.25, 52121.74) * mm, "end": v(57345.7, 52125.5) * mm});
            skLineSegment(sketch, "E287", {"start": v(57345.7, 52125.5) * mm, "end": v(57392.04, 51972.37) * mm});
            skLineSegment(sketch, "E288", {"start": v(57392.04, 51972.37) * mm, "end": v(57379.6, 51968.6) * mm});
            skLineSegment(sketch, "E289", {"start": v(57379.6, 51968.6) * mm, "end": v(57361.93, 52026.98) * mm});
            skArc(sketch, "E290", {"start": v(57361.93, 52026.98) * mm, "mid": v(57354.65, 52035.86) * mm, "end": v(57343.23, 52037) * mm});
            skLineSegment(sketch, "E291", {"start": v(57343.23, 52037) * mm, "end": v(57243.69, 52006.87) * mm});
            skArc(sketch, "E292", {"start": v(57243.69, 52006.87) * mm, "mid": v(57234.8, 51999.59) * mm, "end": v(57233.68, 51988.17) * mm});
            skLineSegment(sketch, "E293", {"start": v(57233.68, 51988.17) * mm, "end": v(57251.35, 51929.78) * mm});
            skCircle(sketch, "E294", {"center": v(57343, 51858.26) * mm, "radius": 10 * mm});
            skCircle(sketch, "E295", {"center": v(57124.8, 51975.06) * mm, "radius": 10 * mm});
            skCircle(sketch, "E296", {"center": v(57074.1, 52142.56) * mm, "radius": 10 * mm});
            skCircle(sketch, "E297", {"center": v(57175.5, 51807.57) * mm, "radius": 10 * mm});
            skCircle(sketch, "E298", {"center": v(57510.5, 51908.96) * mm, "radius": 10 * mm});
            skCircle(sketch, "E299", {"center": v(57409.1, 52243.95) * mm, "radius": 10 * mm});
            skCircle(sketch, "E300", {"center": v(57241.6, 52193.26) * mm, "radius": 10 * mm});
            skCircle(sketch, "E301", {"center": v(57459.8, 52076.46) * mm, "radius": 10 * mm});
            skLineSegment(sketch, "E302", {"start": v(57579.07, 51872.25) * mm, "end": v(57138.8, 51739) * mm});
            skLineSegment(sketch, "E303", {"start": v(57445.8, 52312.53) * mm, "end": v(57579.07, 51872.25) * mm});
            skLineSegment(sketch, "E304", {"start": v(57005.53, 52179.27) * mm, "end": v(57445.8, 52312.53) * mm});
            skLineSegment(sketch, "E305", {"start": v(57138.8, 51739) * mm, "end": v(57005.53, 52179.27) * mm});
            skLineSegment(sketch, "E306", {"start": v(54035.43, 50956.41) * mm, "end": v(54022.98, 50952.65) * mm});
            skLineSegment(sketch, "E307", {"start": v(54022.98, 50952.65) * mm, "end": v(53976.63, 51105.79) * mm});
            skLineSegment(sketch, "E308", {"start": v(53976.63, 51105.79) * mm, "end": v(53989.08, 51109.55) * mm});
            skLineSegment(sketch, "E309", {"start": v(53989.08, 51109.55) * mm, "end": v(54006.75, 51051.17) * mm});
            skArc(sketch, "E310", {"start": v(54006.75, 51051.17) * mm, "mid": v(54014.02, 51042.29) * mm, "end": v(54025.45, 51041.16) * mm});
            skLineSegment(sketch, "E311", {"start": v(54025.45, 51041.16) * mm, "end": v(54124.99, 51071.28) * mm});
            skArc(sketch, "E312", {"start": v(54124.99, 51071.28) * mm, "mid": v(54133.87, 51078.56) * mm, "end": v(54135, 51089.99) * mm});
            skLineSegment(sketch, "E313", {"start": v(54135, 51089.99) * mm, "end": v(54117.33, 51148.37) * mm});
            skLineSegment(sketch, "E314", {"start": v(54117.33, 51148.37) * mm, "end": v(54129.77, 51152.14) * mm});
            skLineSegment(sketch, "E315", {"start": v(54129.77, 51152.14) * mm, "end": v(54176.12, 50999) * mm});
            skLineSegment(sketch, "E316", {"start": v(54176.12, 50999) * mm, "end": v(54163.68, 50995.23) * mm});
            skLineSegment(sketch, "E317", {"start": v(54163.68, 50995.23) * mm, "end": v(54146, 51053.62) * mm});
            skArc(sketch, "E318", {"start": v(54146, 51053.62) * mm, "mid": v(54138.73, 51062.5) * mm, "end": v(54127.3, 51063.63) * mm});
            skLineSegment(sketch, "E319", {"start": v(54127.3, 51063.63) * mm, "end": v(54027.77, 51033.5) * mm});
            skArc(sketch, "E320", {"start": v(54027.77, 51033.5) * mm, "mid": v(54018.89, 51026.22) * mm, "end": v(54017.75, 51014.8) * mm});
            skLineSegment(sketch, "E321", {"start": v(54017.75, 51014.8) * mm, "end": v(54035.43, 50956.41) * mm});
            skCircle(sketch, "E322", {"center": v(54127.07, 50884.9) * mm, "radius": 10 * mm});
            skCircle(sketch, "E323", {"center": v(53908.88, 51001.7) * mm, "radius": 10 * mm});
            skCircle(sketch, "E324", {"center": v(53858.19, 51169.2) * mm, "radius": 10 * mm});
            skCircle(sketch, "E325", {"center": v(53959.58, 50834.2) * mm, "radius": 10 * mm});
            skCircle(sketch, "E326", {"center": v(54294.57, 50935.6) * mm, "radius": 10 * mm});
            skCircle(sketch, "E327", {"center": v(54193.18, 51270.58) * mm, "radius": 10 * mm});
            skCircle(sketch, "E328", {"center": v(54025.68, 51219.89) * mm, "radius": 10 * mm});
            skCircle(sketch, "E329", {"center": v(54243.87, 51103.09) * mm, "radius": 10 * mm});
            skLineSegment(sketch, "E330", {"start": v(54363.14, 50898.88) * mm, "end": v(53922.87, 50765.62) * mm});
            skLineSegment(sketch, "E331", {"start": v(54229.89, 51339.16) * mm, "end": v(54363.14, 50898.88) * mm});
            skLineSegment(sketch, "E332", {"start": v(53789.61, 51205.9) * mm, "end": v(54229.89, 51339.16) * mm});
            skLineSegment(sketch, "E333", {"start": v(53922.87, 50765.62) * mm, "end": v(53789.61, 51205.9) * mm});
            skLineSegment(sketch, "E334", {"start": v(52250.92, 56852.27) * mm, "end": v(52238.47, 56848.5) * mm});
            skLineSegment(sketch, "E335", {"start": v(52238.47, 56848.5) * mm, "end": v(52192.12, 57001.64) * mm});
            skLineSegment(sketch, "E336", {"start": v(52192.12, 57001.64) * mm, "end": v(52204.57, 57005.4) * mm});
            skLineSegment(sketch, "E337", {"start": v(52204.57, 57005.4) * mm, "end": v(52222.24, 56947.02) * mm});
            skArc(sketch, "E338", {"start": v(52222.24, 56947.02) * mm, "mid": v(52229.51, 56938.14) * mm, "end": v(52240.94, 56937.01) * mm});
            skLineSegment(sketch, "E339", {"start": v(52240.94, 56937.01) * mm, "end": v(52340.48, 56967.14) * mm});
            skArc(sketch, "E340", {"start": v(52340.48, 56967.14) * mm, "mid": v(52349.36, 56974.42) * mm, "end": v(52350.5, 56985.84) * mm});
            skLineSegment(sketch, "E341", {"start": v(52350.5, 56985.84) * mm, "end": v(52332.82, 57044.23) * mm});
            skLineSegment(sketch, "E342", {"start": v(52332.82, 57044.23) * mm, "end": v(52345.26, 57048) * mm});
            skLineSegment(sketch, "E343", {"start": v(52345.26, 57048) * mm, "end": v(52391.61, 56894.85) * mm});
            skLineSegment(sketch, "E344", {"start": v(52391.61, 56894.85) * mm, "end": v(52379.17, 56891.09) * mm});
            skLineSegment(sketch, "E345", {"start": v(52379.17, 56891.09) * mm, "end": v(52361.5, 56949.47) * mm});
            skArc(sketch, "E346", {"start": v(52361.5, 56949.47) * mm, "mid": v(52354.22, 56958.35) * mm, "end": v(52342.8, 56959.48) * mm});
            skLineSegment(sketch, "E347", {"start": v(52342.8, 56959.48) * mm, "end": v(52243.26, 56929.36) * mm});
            skArc(sketch, "E348", {"start": v(52243.26, 56929.36) * mm, "mid": v(52234.38, 56922.08) * mm, "end": v(52233.25, 56910.65) * mm});
            skLineSegment(sketch, "E349", {"start": v(52233.25, 56910.65) * mm, "end": v(52250.92, 56852.27) * mm});
            skCircle(sketch, "E350", {"center": v(52342.56, 56780.75) * mm, "radius": 10 * mm});
            skCircle(sketch, "E351", {"center": v(52124.37, 56897.55) * mm, "radius": 10 * mm});
            skCircle(sketch, "E352", {"center": v(52073.68, 57065.05) * mm, "radius": 10 * mm});
            skCircle(sketch, "E353", {"center": v(52175.07, 56730.06) * mm, "radius": 10 * mm});
            skCircle(sketch, "E354", {"center": v(52510.06, 56831.45) * mm, "radius": 10 * mm});
            skCircle(sketch, "E355", {"center": v(52408.67, 57166.44) * mm, "radius": 10 * mm});
            skCircle(sketch, "E356", {"center": v(52241.17, 57115.74) * mm, "radius": 10 * mm});
            skCircle(sketch, "E357", {"center": v(52459.36, 56998.94) * mm, "radius": 10 * mm});
            skLineSegment(sketch, "E358", {"start": v(52578.64, 56794.74) * mm, "end": v(52138.36, 56661.48) * mm});
            skLineSegment(sketch, "E359", {"start": v(52445.38, 57235.01) * mm, "end": v(52578.64, 56794.74) * mm});
            skLineSegment(sketch, "E360", {"start": v(52005.1, 57101.76) * mm, "end": v(52445.38, 57235.01) * mm});
            skLineSegment(sketch, "E361", {"start": v(52138.36, 56661.48) * mm, "end": v(52005.1, 57101.76) * mm});
            skLineSegment(sketch, "E362", {"start": v(55466.84, 57825.64) * mm, "end": v(55454.4, 57821.87) * mm});
            skLineSegment(sketch, "E363", {"start": v(55454.4, 57821.87) * mm, "end": v(55408.04, 57975.01) * mm});
            skLineSegment(sketch, "E364", {"start": v(55408.04, 57975.01) * mm, "end": v(55420.49, 57978.78) * mm});
            skLineSegment(sketch, "E365", {"start": v(55420.49, 57978.78) * mm, "end": v(55438.16, 57920.4) * mm});
            skArc(sketch, "E366", {"start": v(55438.16, 57920.4) * mm, "mid": v(55445.44, 57911.51) * mm, "end": v(55456.86, 57910.38) * mm});
            skLineSegment(sketch, "E367", {"start": v(55456.86, 57910.38) * mm, "end": v(55556.4, 57940.5) * mm});
            skArc(sketch, "E368", {"start": v(55556.4, 57940.5) * mm, "mid": v(55565.28, 57947.79) * mm, "end": v(55566.41, 57959.21) * mm});
            skLineSegment(sketch, "E369", {"start": v(55566.41, 57959.21) * mm, "end": v(55548.74, 58017.6) * mm});
            skLineSegment(sketch, "E370", {"start": v(55548.74, 58017.6) * mm, "end": v(55561.18, 58021.36) * mm});
            skLineSegment(sketch, "E371", {"start": v(55561.18, 58021.36) * mm, "end": v(55607.53, 57868.22) * mm});
            skLineSegment(sketch, "E372", {"start": v(55607.53, 57868.22) * mm, "end": v(55595.1, 57864.46) * mm});
            skLineSegment(sketch, "E373", {"start": v(55595.1, 57864.46) * mm, "end": v(55577.42, 57922.84) * mm});
            skArc(sketch, "E374", {"start": v(55577.42, 57922.84) * mm, "mid": v(55570.14, 57931.72) * mm, "end": v(55558.72, 57932.85) * mm});
            skLineSegment(sketch, "E375", {"start": v(55558.72, 57932.85) * mm, "end": v(55459.18, 57902.72) * mm});
            skArc(sketch, "E376", {"start": v(55459.18, 57902.72) * mm, "mid": v(55450.3, 57895.45) * mm, "end": v(55449.17, 57884.02) * mm});
            skLineSegment(sketch, "E377", {"start": v(55449.17, 57884.02) * mm, "end": v(55466.84, 57825.64) * mm});
            skCircle(sketch, "E378", {"center": v(55558.49, 57754.12) * mm, "radius": 10 * mm});
            skCircle(sketch, "E379", {"center": v(55340.3, 57870.92) * mm, "radius": 10 * mm});
            skCircle(sketch, "E380", {"center": v(55289.6, 58038.42) * mm, "radius": 10 * mm});
            skCircle(sketch, "E381", {"center": v(55391, 57703.42) * mm, "radius": 10 * mm});
            skCircle(sketch, "E382", {"center": v(55725.98, 57804.82) * mm, "radius": 10 * mm});
            skCircle(sketch, "E383", {"center": v(55624.59, 58139.8) * mm, "radius": 10 * mm});
            skCircle(sketch, "E384", {"center": v(55457.1, 58089.11) * mm, "radius": 10 * mm});
            skCircle(sketch, "E385", {"center": v(55675.29, 57972.31) * mm, "radius": 10 * mm});
            skLineSegment(sketch, "E386", {"start": v(55794.56, 57768.1) * mm, "end": v(55354.28, 57634.85) * mm});
            skLineSegment(sketch, "E387", {"start": v(55661.3, 58208.38) * mm, "end": v(55794.56, 57768.1) * mm});
            skLineSegment(sketch, "E388", {"start": v(55221.02, 58075.12) * mm, "end": v(55661.3, 58208.38) * mm});
            skLineSegment(sketch, "E389", {"start": v(55354.28, 57634.85) * mm, "end": v(55221.02, 58075.12) * mm});
            skLineSegment(sketch, "E390", {"start": v(54409.66, 51283.84) * mm, "end": v(52697.54, 56940.4) * mm});
            skLineSegment(sketch, "E391", {"start": v(52697.54, 56940.4) * mm, "end": v(55174.56, 57690.15) * mm});
            skLineSegment(sketch, "E392", {"start": v(55174.56, 57690.15) * mm, "end": v(56886.68, 52033.59) * mm});
            skLineSegment(sketch, "E393", {"start": v(56886.68, 52033.59) * mm, "end": v(54409.66, 51283.84) * mm});
            skLineSegment(sketch, "E394", {"start": v(39664.12, 55944.6) * mm, "end": v(40724.15, 52442.47) * mm});
            skLineSegment(sketch, "E395", {"start": v(38916.03, 56345.06) * mm, "end": v(39976, 52843.08) * mm});
            skLineSegment(sketch, "E396", {"start": v(40724.15, 52442.47) * mm, "end": v(36317.17, 51109.92) * mm});
            skLineSegment(sketch, "E397", {"start": v(39976, 52843.08) * mm, "end": v(36717.67, 51857.85) * mm});
            skLineSegment(sketch, "E398", {"start": v(30437.41, 72606.72) * mm, "end": v(36717.67, 51857.85) * mm});
            skLineSegment(sketch, "E399", {"start": v(29657.7, 73111.61) * mm, "end": v(36317.17, 51109.92) * mm});
            skLineSegment(sketch, "E400", {"start": v(38916.03, 56345.06) * mm, "end": v(44311.28, 57978.1) * mm});
            skLineSegment(sketch, "E401", {"start": v(44485.1, 57403.82) * mm, "end": v(44311.28, 57978.1) * mm});
            skLineSegment(sketch, "E402", {"start": v(39664.12, 55944.6) * mm, "end": v(44485.1, 57403.82) * mm});
            skLineSegment(sketch, "E403", {"start": v(29657.7, 73111.61) * mm, "end": v(53564.5, 76178.39) * mm});
            skLineSegment(sketch, "E404", {"start": v(30437.41, 72606.72) * mm, "end": v(53235.88, 75531.31) * mm});
            skLineSegment(sketch, "E405", {"start": v(68033.92, 49903.52) * mm, "end": v(54030.97, 45665.1) * mm});
            skLineSegment(sketch, "E406", {"start": v(67150.92, 50263.13) * mm, "end": v(54431.42, 46413.2) * mm});
            skLineSegment(sketch, "E407", {"start": v(54030.97, 45665.1) * mm, "end": v(49801.13, 59639.76) * mm});
            skLineSegment(sketch, "E408", {"start": v(50375.4, 59813.58) * mm, "end": v(49801.13, 59639.76) * mm});
            skLineSegment(sketch, "E409", {"start": v(54431.42, 46413.2) * mm, "end": v(50375.4, 59813.58) * mm});
            skLineSegment(sketch, "E410", {"start": v(53564.5, 76178.39) * mm, "end": v(68033.92, 49903.52) * mm});
            skLineSegment(sketch, "E411", {"start": v(53235.88, 75531.31) * mm, "end": v(67150.92, 50263.13) * mm});
            skLineSegment(sketch, "E412", {"start": v(43746.98, 61568.38) * mm, "end": v(39705.16, 60345.03) * mm});
            skLineSegment(sketch, "E413", {"start": v(39705.16, 60345.03) * mm, "end": v(39792.07, 60057.9) * mm});
            skLineSegment(sketch, "E414", {"start": v(39792.07, 60057.9) * mm, "end": v(43833.9, 61281.24) * mm});
            skLineSegment(sketch, "E415", {"start": v(43833.9, 61281.24) * mm, "end": v(43746.98, 61568.38) * mm});
            skLineSegment(sketch, "E416", {"start": v(41296.56, 69605.87) * mm, "end": v(42482.87, 61185.76) * mm});
            skLineSegment(sketch, "E417", {"start": v(48359.31, 61648.42) * mm, "end": v(47221.03, 70350.15) * mm});
            skLineSegment(sketch, "E418", {"start": v(46847.5, 70314.47) * mm, "end": v(47995.52, 61538.3) * mm});
            skLineSegment(sketch, "E419", {"start": v(55724.5, 60181.57) * mm, "end": v(50819.09, 58696.48) * mm});
            skLineSegment(sketch, "E420", {"start": v(49204.3, 59986.36) * mm, "end": v(54308.63, 61531.67) * mm});
            skLineSegment(sketch, "E421", {"start": v(48048.78, 64022.34) * mm, "end": v(52784.2, 65455.66) * mm});
            skLineSegment(sketch, "E422", {"start": v(52597.15, 65791.14) * mm, "end": v(47999.48, 64399.22) * mm});
            skLineSegment(sketch, "E423", {"start": v(54200, 61890.59) * mm, "end": v(49095.75, 60345.3) * mm});
            skLineSegment(sketch, "E424", {"start": v(32737.3, 66492.66) * mm, "end": v(35570.65, 67350.91) * mm});
            skLineSegment(sketch, "E425", {"start": v(37393.76, 61301.44) * mm, "end": v(35125.04, 68796.87) * mm});
            skLineSegment(sketch, "E426", {"start": v(37752.67, 61410.08) * mm, "end": v(35484.16, 68904.97) * mm});
            skLineSegment(sketch, "E427", {"start": v(32850.1, 66135) * mm, "end": v(35679.29, 66991.99) * mm});
            skLineSegment(sketch, "E428", {"start": v(59287.5, 52158.7) * mm, "end": v(60066.85, 52394.65) * mm});
            skLineSegment(sketch, "E429", {"start": v(57364.27, 55607.68) * mm, "end": v(58143.3, 55843.53) * mm});
            skLineSegment(sketch, "E430", {"start": v(41667.9, 69658.19) * mm, "end": v(42846.14, 61295.28) * mm});
            skLineSegment(sketch, "E431", {"start": v(37539.24, 62141.45) * mm, "end": v(41560.53, 67604.46) * mm});
            skLineSegment(sketch, "E432", {"start": v(41650.45, 67094.03) * mm, "end": v(37674.97, 61693.26) * mm});
            skLineSegment(sketch, "E433", {"start": v(31997.32, 72403.55) * mm, "end": v(33353.34, 67923.5) * mm});
            skLineSegment(sketch, "E434", {"start": v(40437.2, 70067.64) * mm, "end": v(39441.15, 73358.44) * mm});
            skLineSegment(sketch, "E435", {"start": v(33353.34, 67923.5) * mm, "end": v(40437.2, 70067.64) * mm});
            skLineSegment(sketch, "E436", {"start": v(38520.96, 69487.63) * mm, "end": v(38047.53, 73179.67) * mm});
            skLineSegment(sketch, "E437", {"start": v(38812.11, 69575.76) * mm, "end": v(38345.1, 73217.85) * mm});
            skLineSegment(sketch, "E438", {"start": v(35107.62, 70149.24) * mm, "end": v(34334.2, 72704.48) * mm});
            skLineSegment(sketch, "E439", {"start": v(34820.49, 70062.33) * mm, "end": v(34032.47, 72665.79) * mm});
            skLineSegment(sketch, "E440", {"start": v(35803.5, 68665.12) * mm, "end": v(35270.3, 72823.4) * mm});
            skLineSegment(sketch, "E441", {"start": v(36094.66, 68753.24) * mm, "end": v(35567.85, 72861.58) * mm});
            skLineSegment(sketch, "E442", {"start": v(39792.07, 60057.9) * mm, "end": v(38292.07, 59603.88) * mm});
            skLineSegment(sketch, "E443", {"start": v(39705.16, 60345.03) * mm, "end": v(38205.16, 59891.02) * mm});
            skLineSegment(sketch, "E444", {"start": v(48417.7, 61733.56) * mm, "end": v(53758.17, 63350.02) * mm});
            skLineSegment(sketch, "E445", {"start": v(48798.71, 61326.49) * mm, "end": v(53903.04, 62871.46) * mm});
            skLineSegment(sketch, "E446", {"start": v(35125.2, 68796.33) * mm, "end": v(35484.16, 68904.97) * mm});
            skLineSegment(sketch, "E447", {"start": v(37391.17, 61300.66) * mm, "end": v(37750.12, 61409.3) * mm});
            skLineSegment(sketch, "E448", {"start": v(64765.56, 53744.58) * mm, "end": v(64866.07, 53800.47) * mm});
            skLineSegment(sketch, "E449", {"start": v(64866.07, 53800.47) * mm, "end": v(65157.68, 53276.1) * mm});
            skLineSegment(sketch, "E450", {"start": v(65157.68, 53276.1) * mm, "end": v(65057.18, 53220.21) * mm});
            skLineSegment(sketch, "E451", {"start": v(65057.18, 53220.21) * mm, "end": v(64765.56, 53744.58) * mm});
            skLineSegment(sketch, "E452", {"start": v(30437.41, 72606.72) * mm, "end": v(53075.2, 75510.7) * mm});
            skLineSegment(sketch, "E453", {"start": v(30957.21, 72270.12) * mm, "end": v(52857.63, 75079.51) * mm});
            skLineSegment(sketch, "E454", {"start": v(53075.2, 75510.7) * mm, "end": v(67150.92, 50263.13) * mm});
            skLineSegment(sketch, "E455", {"start": v(52857.63, 75079.51) * mm, "end": v(66559.72, 50502.1) * mm});
            skLineSegment(sketch, "E456", {"start": v(67150.92, 50263.13) * mm, "end": v(54145.32, 46326.6) * mm});
            skLineSegment(sketch, "E457", {"start": v(66559.72, 50502.1) * mm, "end": v(54412.29, 46825.33) * mm});
            skLineSegment(sketch, "E458", {"start": v(54145.32, 46326.6) * mm, "end": v(50089.3, 59726.98) * mm});
            skLineSegment(sketch, "E459", {"start": v(54412.29, 46825.33) * mm, "end": v(50356.27, 60225.7) * mm});
            skLineSegment(sketch, "E460", {"start": v(50089.3, 59726.98) * mm, "end": v(49336.06, 59499) * mm});
            skLineSegment(sketch, "E461", {"start": v(49220.18, 59881.84) * mm, "end": v(49336.06, 59499) * mm});
            skLineSegment(sketch, "E462", {"start": v(50356.27, 60225.7) * mm, "end": v(49220.18, 59881.84) * mm});
            skLineSegment(sketch, "E463", {"start": v(39517.02, 53123.18) * mm, "end": v(38573.23, 56241.3) * mm});
            skLineSegment(sketch, "E464", {"start": v(39977.46, 52844.63) * mm, "end": v(38917.8, 56345.6) * mm});
            skLineSegment(sketch, "E465", {"start": v(35924.94, 55857.64) * mm, "end": v(44386.82, 58418.88) * mm});
            skLineSegment(sketch, "E466", {"start": v(44502.7, 58036.03) * mm, "end": v(44386.82, 58418.88) * mm});
            skLineSegment(sketch, "E467", {"start": v(38917.8, 56345.6) * mm, "end": v(44502.7, 58036.03) * mm});
            skLineSegment(sketch, "E468", {"start": v(36040.82, 55474.8) * mm, "end": v(38573.23, 56241.3) * mm});
            skLineSegment(sketch, "E469", {"start": v(30957.21, 72270.12) * mm, "end": v(36984.61, 52356.67) * mm});
            skLineSegment(sketch, "E470", {"start": v(36040.82, 55474.8) * mm, "end": v(36984.61, 52356.67) * mm});
            skLineSegment(sketch, "E471", {"start": v(30437.41, 72606.72) * mm, "end": v(36717.64, 51857.95) * mm});
            skLineSegment(sketch, "E472", {"start": v(30957.21, 72270.12) * mm, "end": v(35924.94, 55857.64) * mm});
            skLineSegment(sketch, "E473", {"start": v(36984.61, 52356.67) * mm, "end": v(39517.02, 53123.18) * mm});
            skLineSegment(sketch, "E474", {"start": v(36717.64, 51857.95) * mm, "end": v(39977.46, 52844.63) * mm});
            skCircle(sketch, "E475", {"center": v(53400.19, 75854.85) * mm, "radius": 300 * mm});
            skLineSegment(sketch, "E476", {"start": v(53400.19, 75854.85) * mm, "end": v(67780.92, 49741.01) * mm});
            skCircle(sketch, "E477", {"center": v(53759.7, 75202) * mm, "radius": 300 * mm});
            skCircle(sketch, "E478", {"center": v(54119.23, 74549.16) * mm, "radius": 300 * mm});
            skCircle(sketch, "E479", {"center": v(54478.74, 73896.31) * mm, "radius": 300 * mm});
            skCircle(sketch, "E480", {"center": v(54838.26, 73243.47) * mm, "radius": 300 * mm});
            skCircle(sketch, "E481", {"center": v(55197.78, 72590.62) * mm, "radius": 300 * mm});
            skCircle(sketch, "E482", {"center": v(55557.3, 71937.77) * mm, "radius": 300 * mm});
            skCircle(sketch, "E483", {"center": v(55916.82, 71284.93) * mm, "radius": 300 * mm});
            skCircle(sketch, "E484", {"center": v(56276.34, 70632.08) * mm, "radius": 300 * mm});
            skCircle(sketch, "E485", {"center": v(56635.85, 69979.24) * mm, "radius": 300 * mm});
            skCircle(sketch, "E486", {"center": v(56995.37, 69326.4) * mm, "radius": 300 * mm});
            skCircle(sketch, "E487", {"center": v(57354.9, 68673.55) * mm, "radius": 300 * mm});
            skCircle(sketch, "E488", {"center": v(57714.4, 68020.7) * mm, "radius": 300 * mm});
            skCircle(sketch, "E489", {"center": v(58073.93, 67367.85) * mm, "radius": 300 * mm});
            skCircle(sketch, "E490", {"center": v(58433.45, 66715) * mm, "radius": 300 * mm});
            skCircle(sketch, "E491", {"center": v(58792.97, 66062.16) * mm, "radius": 300 * mm});
            skCircle(sketch, "E492", {"center": v(59152.48, 65409.32) * mm, "radius": 300 * mm});
            skCircle(sketch, "E493", {"center": v(59512, 64756.47) * mm, "radius": 300 * mm});
            skCircle(sketch, "E494", {"center": v(59871.52, 64103.62) * mm, "radius": 300 * mm});
            skCircle(sketch, "E495", {"center": v(60231.04, 63450.78) * mm, "radius": 300 * mm});
            skCircle(sketch, "E496", {"center": v(60590.56, 62797.93) * mm, "radius": 300 * mm});
            skCircle(sketch, "E497", {"center": v(60950.08, 62145.09) * mm, "radius": 300 * mm});
            skCircle(sketch, "E498", {"center": v(61309.6, 61492.24) * mm, "radius": 300 * mm});
            skCircle(sketch, "E499", {"center": v(61669.11, 60839.4) * mm, "radius": 300 * mm});
            skCircle(sketch, "E500", {"center": v(62028.63, 60186.55) * mm, "radius": 300 * mm});
            skCircle(sketch, "E501", {"center": v(62388.15, 59533.7) * mm, "radius": 300 * mm});
            skCircle(sketch, "E502", {"center": v(62747.67, 58880.86) * mm, "radius": 300 * mm});
            skCircle(sketch, "E503", {"center": v(63107.19, 58228.01) * mm, "radius": 300 * mm});
            skCircle(sketch, "E504", {"center": v(63466.7, 57575.16) * mm, "radius": 300 * mm});
            skCircle(sketch, "E505", {"center": v(63826.22, 56922.32) * mm, "radius": 300 * mm});
            skCircle(sketch, "E506", {"center": v(64185.74, 56269.47) * mm, "radius": 300 * mm});
            skCircle(sketch, "E507", {"center": v(64545.26, 55616.63) * mm, "radius": 300 * mm});
            skCircle(sketch, "E508", {"center": v(64904.78, 54963.78) * mm, "radius": 300 * mm});
            skCircle(sketch, "E509", {"center": v(65264.3, 54310.94) * mm, "radius": 300 * mm});
            skCircle(sketch, "E510", {"center": v(65623.81, 53658.09) * mm, "radius": 300 * mm});
            skCircle(sketch, "E511", {"center": v(65983.33, 53005.24) * mm, "radius": 300 * mm});
            skCircle(sketch, "E512", {"center": v(66342.85, 52352.4) * mm, "radius": 300 * mm});
            skCircle(sketch, "E513", {"center": v(66702.37, 51699.55) * mm, "radius": 300 * mm});
            skCircle(sketch, "E514", {"center": v(67061.89, 51046.7) * mm, "radius": 300 * mm});
            skCircle(sketch, "E515", {"center": v(67421.4, 50393.86) * mm, "radius": 300 * mm});
            skCircle(sketch, "E516", {"center": v(67824.74, 49764.95) * mm, "radius": 300 * mm});
            skCircle(sketch, "E517", {"center": v(53939.47, 74875.58) * mm, "radius": 300 * mm});
            skCircle(sketch, "E518", {"center": v(54298.99, 74222.74) * mm, "radius": 300 * mm});
            skCircle(sketch, "E519", {"center": v(54658.5, 73569.89) * mm, "radius": 300 * mm});
            skCircle(sketch, "E520", {"center": v(55018.02, 72917.04) * mm, "radius": 300 * mm});
            skCircle(sketch, "E521", {"center": v(55377.54, 72264.2) * mm, "radius": 300 * mm});
            skCircle(sketch, "E522", {"center": v(55737.06, 71611.35) * mm, "radius": 300 * mm});
            skCircle(sketch, "E523", {"center": v(56096.58, 70958.5) * mm, "radius": 300 * mm});
            skCircle(sketch, "E524", {"center": v(56456.1, 70305.66) * mm, "radius": 300 * mm});
            skCircle(sketch, "E525", {"center": v(56815.61, 69652.81) * mm, "radius": 300 * mm});
            skCircle(sketch, "E526", {"center": v(57175.13, 68999.97) * mm, "radius": 300 * mm});
            skCircle(sketch, "E527", {"center": v(57534.65, 68347.12) * mm, "radius": 300 * mm});
            skCircle(sketch, "E528", {"center": v(57894.17, 67694.28) * mm, "radius": 300 * mm});
            skCircle(sketch, "E529", {"center": v(58253.69, 67041.43) * mm, "radius": 300 * mm});
            skCircle(sketch, "E530", {"center": v(58613.2, 66388.58) * mm, "radius": 300 * mm});
            skCircle(sketch, "E531", {"center": v(58972.72, 65735.74) * mm, "radius": 300 * mm});
            skCircle(sketch, "E532", {"center": v(59332.24, 65082.9) * mm, "radius": 300 * mm});
            skCircle(sketch, "E533", {"center": v(59691.76, 64430.05) * mm, "radius": 300 * mm});
            skCircle(sketch, "E534", {"center": v(60051.28, 63777.2) * mm, "radius": 300 * mm});
            skCircle(sketch, "E535", {"center": v(60410.8, 63124.35) * mm, "radius": 300 * mm});
            skCircle(sketch, "E536", {"center": v(60770.32, 62471.5) * mm, "radius": 300 * mm});
            skCircle(sketch, "E537", {"center": v(61129.83, 61818.66) * mm, "radius": 300 * mm});
            skCircle(sketch, "E538", {"center": v(61489.35, 61165.82) * mm, "radius": 300 * mm});
            skCircle(sketch, "E539", {"center": v(61848.87, 60512.97) * mm, "radius": 300 * mm});
            skCircle(sketch, "E540", {"center": v(62208.39, 59860.13) * mm, "radius": 300 * mm});
            skCircle(sketch, "E541", {"center": v(62567.9, 59207.28) * mm, "radius": 300 * mm});
            skCircle(sketch, "E542", {"center": v(62927.43, 58554.43) * mm, "radius": 300 * mm});
            skCircle(sketch, "E543", {"center": v(63286.94, 57901.59) * mm, "radius": 300 * mm});
            skCircle(sketch, "E544", {"center": v(63646.46, 57248.74) * mm, "radius": 300 * mm});
            skCircle(sketch, "E545", {"center": v(64005.98, 56595.9) * mm, "radius": 300 * mm});
            skCircle(sketch, "E546", {"center": v(64725.02, 55290.2) * mm, "radius": 300 * mm});
            skCircle(sketch, "E547", {"center": v(65084.54, 54637.36) * mm, "radius": 300 * mm});
            skCircle(sketch, "E548", {"center": v(65444.05, 53984.51) * mm, "radius": 300 * mm});
            skCircle(sketch, "E549", {"center": v(64365.5, 55943.05) * mm, "radius": 300 * mm});
            skCircle(sketch, "E550", {"center": v(65803.57, 53331.67) * mm, "radius": 300 * mm});
            skCircle(sketch, "E551", {"center": v(66163.1, 52678.82) * mm, "radius": 300 * mm});
            skCircle(sketch, "E552", {"center": v(66882.13, 51373.13) * mm, "radius": 300 * mm});
            skCircle(sketch, "E553", {"center": v(67241.65, 50720.28) * mm, "radius": 300 * mm});
            skCircle(sketch, "E554", {"center": v(66522.61, 52025.97) * mm, "radius": 300 * mm});
            skCircle(sketch, "E555", {"center": v(49888.89, 59352.88) * mm, "radius": 300 * mm});
            skCircle(sketch, "E556", {"center": v(53945.1, 45952.56) * mm, "radius": 300 * mm});
            skCircle(sketch, "E557", {"center": v(30047.42, 72859.15) * mm, "radius": 300 * mm});
            skCircle(sketch, "E558", {"center": v(33293.56, 62134.5) * mm, "radius": 300 * mm});
            skCircle(sketch, "E559", {"center": v(33077.15, 62849.46) * mm, "radius": 300 * mm});
            skCircle(sketch, "E560", {"center": v(32860.74, 63564.43) * mm, "radius": 300 * mm});
            skCircle(sketch, "E561", {"center": v(32644.34, 64279.4) * mm, "radius": 300 * mm});
            skCircle(sketch, "E562", {"center": v(32427.93, 64994.36) * mm, "radius": 300 * mm});
            skCircle(sketch, "E563", {"center": v(32211.53, 65709.33) * mm, "radius": 300 * mm});
            skCircle(sketch, "E564", {"center": v(31995.12, 66424.3) * mm, "radius": 300 * mm});
            skCircle(sketch, "E565", {"center": v(31778.71, 67139.26) * mm, "radius": 300 * mm});
            skCircle(sketch, "E566", {"center": v(31562.3, 67854.23) * mm, "radius": 300 * mm});
            skCircle(sketch, "E567", {"center": v(31345.9, 68569.2) * mm, "radius": 300 * mm});
            skCircle(sketch, "E568", {"center": v(31129.5, 69284.16) * mm, "radius": 300 * mm});
            skCircle(sketch, "E569", {"center": v(30913.1, 69999.13) * mm, "radius": 300 * mm});
            skCircle(sketch, "E570", {"center": v(30696.68, 70714.1) * mm, "radius": 300 * mm});
            skCircle(sketch, "E571", {"center": v(30480.28, 71429.06) * mm, "radius": 300 * mm});
            skCircle(sketch, "E572", {"center": v(30263.87, 72144.03) * mm, "radius": 300 * mm});
            skCircle(sketch, "E573", {"center": v(30777.44, 72952.8) * mm, "radius": 300 * mm});
            skCircle(sketch, "E574", {"center": v(31507.46, 73046.44) * mm, "radius": 300 * mm});
            skCircle(sketch, "E575", {"center": v(32237.47, 73140.09) * mm, "radius": 300 * mm});
            skCircle(sketch, "E576", {"center": v(32967.5, 73233.74) * mm, "radius": 300 * mm});
            skCircle(sketch, "E577", {"center": v(33697.51, 73327.38) * mm, "radius": 300 * mm});
            skCircle(sketch, "E578", {"center": v(34427.53, 73421.03) * mm, "radius": 300 * mm});
            skCircle(sketch, "E579", {"center": v(35157.55, 73514.68) * mm, "radius": 300 * mm});
            skCircle(sketch, "E580", {"center": v(35887.56, 73608.32) * mm, "radius": 300 * mm});
            skCircle(sketch, "E581", {"center": v(36617.58, 73701.97) * mm, "radius": 300 * mm});
            skCircle(sketch, "E582", {"center": v(37347.6, 73795.62) * mm, "radius": 300 * mm});
            skCircle(sketch, "E583", {"center": v(38077.62, 73889.27) * mm, "radius": 300 * mm});
            skCircle(sketch, "E584", {"center": v(38807.64, 73982.91) * mm, "radius": 300 * mm});
            skCircle(sketch, "E585", {"center": v(39537.65, 74076.56) * mm, "radius": 300 * mm});
            skCircle(sketch, "E586", {"center": v(40267.67, 74170.2) * mm, "radius": 300 * mm});
            skCircle(sketch, "E587", {"center": v(40997.7, 74263.85) * mm, "radius": 300 * mm});
            skCircle(sketch, "E588", {"center": v(41727.7, 74357.5) * mm, "radius": 300 * mm});
            skCircle(sketch, "E589", {"center": v(42457.73, 74451.15) * mm, "radius": 300 * mm});
            skCircle(sketch, "E590", {"center": v(43187.74, 74544.8) * mm, "radius": 300 * mm});
            skCircle(sketch, "E591", {"center": v(43917.76, 74638.44) * mm, "radius": 300 * mm});
            skCircle(sketch, "E592", {"center": v(44647.78, 74732.09) * mm, "radius": 300 * mm});
            skCircle(sketch, "E593", {"center": v(45377.8, 74825.74) * mm, "radius": 300 * mm});
            skCircle(sketch, "E594", {"center": v(46107.82, 74919.38) * mm, "radius": 300 * mm});
            skCircle(sketch, "E595", {"center": v(46837.83, 75013.03) * mm, "radius": 300 * mm});
            skCircle(sketch, "E596", {"center": v(47567.85, 75106.68) * mm, "radius": 300 * mm});
            skCircle(sketch, "E597", {"center": v(48297.87, 75200.32) * mm, "radius": 300 * mm});
            skCircle(sketch, "E598", {"center": v(49027.89, 75293.97) * mm, "radius": 300 * mm});
            skCircle(sketch, "E599", {"center": v(49757.9, 75387.62) * mm, "radius": 300 * mm});
            skCircle(sketch, "E600", {"center": v(50487.92, 75481.26) * mm, "radius": 300 * mm});
            skCircle(sketch, "E601", {"center": v(51217.94, 75574.91) * mm, "radius": 300 * mm});
            skCircle(sketch, "E602", {"center": v(51947.96, 75668.56) * mm, "radius": 300 * mm});
            skCircle(sketch, "E603", {"center": v(52677.98, 75762.2) * mm, "radius": 300 * mm});
            skCircle(sketch, "E604", {"center": v(54664.85, 46170.41) * mm, "radius": 300 * mm});
            skCircle(sketch, "E605", {"center": v(55384.6, 46388.28) * mm, "radius": 300 * mm});
            skCircle(sketch, "E606", {"center": v(56104.35, 46606.14) * mm, "radius": 300 * mm});
            skCircle(sketch, "E607", {"center": v(56824.1, 46824) * mm, "radius": 300 * mm});
            skCircle(sketch, "E608", {"center": v(57543.85, 47041.87) * mm, "radius": 300 * mm});
            skCircle(sketch, "E609", {"center": v(58263.6, 47259.73) * mm, "radius": 300 * mm});
            skCircle(sketch, "E610", {"center": v(58983.35, 47477.6) * mm, "radius": 300 * mm});
            skCircle(sketch, "E611", {"center": v(59703.1, 47695.46) * mm, "radius": 300 * mm});
            skCircle(sketch, "E612", {"center": v(60422.84, 47913.33) * mm, "radius": 300 * mm});
            skCircle(sketch, "E613", {"center": v(61142.6, 48131.2) * mm, "radius": 300 * mm});
            skCircle(sketch, "E614", {"center": v(61862.34, 48349.06) * mm, "radius": 300 * mm});
            skCircle(sketch, "E615", {"center": v(62582.1, 48566.92) * mm, "radius": 300 * mm});
            skCircle(sketch, "E616", {"center": v(63301.84, 48784.78) * mm, "radius": 300 * mm});
            skCircle(sketch, "E617", {"center": v(64021.6, 49002.65) * mm, "radius": 300 * mm});
            skCircle(sketch, "E618", {"center": v(64741.34, 49220.51) * mm, "radius": 300 * mm});
            skCircle(sketch, "E619", {"center": v(65461.09, 49438.38) * mm, "radius": 300 * mm});
            skCircle(sketch, "E620", {"center": v(66180.84, 49656.24) * mm, "radius": 300 * mm});
            skCircle(sketch, "E621", {"center": v(53731.58, 46657.95) * mm, "radius": 300 * mm});
            skCircle(sketch, "E622", {"center": v(53518.06, 47363.34) * mm, "radius": 300 * mm});
            skCircle(sketch, "E623", {"center": v(53304.54, 48068.73) * mm, "radius": 300 * mm});
            skCircle(sketch, "E624", {"center": v(53091.02, 48774.13) * mm, "radius": 300 * mm});
            skCircle(sketch, "E625", {"center": v(52877.5, 49479.52) * mm, "radius": 300 * mm});
            skCircle(sketch, "E626", {"center": v(52663.99, 50184.91) * mm, "radius": 300 * mm});
            skCircle(sketch, "E627", {"center": v(52450.47, 50890.3) * mm, "radius": 300 * mm});
            skCircle(sketch, "E628", {"center": v(52236.95, 51595.7) * mm, "radius": 300 * mm});
            skCircle(sketch, "E629", {"center": v(52023.43, 52301.1) * mm, "radius": 300 * mm});
            skCircle(sketch, "E630", {"center": v(51809.91, 53006.48) * mm, "radius": 300 * mm});
            skCircle(sketch, "E631", {"center": v(51596.4, 53711.88) * mm, "radius": 300 * mm});
            skCircle(sketch, "E632", {"center": v(51382.87, 54417.27) * mm, "radius": 300 * mm});
            skCircle(sketch, "E633", {"center": v(51169.35, 55122.66) * mm, "radius": 300 * mm});
            skCircle(sketch, "E634", {"center": v(50955.84, 55828.05) * mm, "radius": 300 * mm});
            skCircle(sketch, "E635", {"center": v(50742.32, 56533.45) * mm, "radius": 300 * mm});
            skCircle(sketch, "E636", {"center": v(50528.8, 57238.84) * mm, "radius": 300 * mm});
            skCircle(sketch, "E637", {"center": v(50315.28, 57944.23) * mm, "radius": 300 * mm});
            skCircle(sketch, "E638", {"center": v(50101.76, 58649.62) * mm, "radius": 300 * mm});
            skLineSegment(sketch, "E639", {"start": v(30047.42, 72859.15) * mm, "end": v(35457.62, 54984.83) * mm});
            skLineSegment(sketch, "E640", {"start": v(53945.1, 45952.56) * mm, "end": v(49888.89, 59352.88) * mm});
            skLineSegment(sketch, "E641", {"start": v(53945.1, 45952.56) * mm, "end": v(66900.59, 49874.1) * mm});
            skLineSegment(sketch, "E642", {"start": v(30047.42, 72859.15) * mm, "end": v(53400.19, 75854.85) * mm});
            skCircle(sketch, "E643", {"center": v(53579.95, 75528.43) * mm, "radius": 300 * mm});
            skCircle(sketch, "E644", {"center": v(40161.14, 53266.98) * mm, "radius": 300 * mm});
            skCircle(sketch, "E645", {"center": v(39509.32, 55420.5) * mm, "radius": 300 * mm});
            skCircle(sketch, "E646", {"center": v(39726.6, 54702.66) * mm, "radius": 300 * mm});
            skCircle(sketch, "E647", {"center": v(39943.87, 53984.82) * mm, "radius": 300 * mm});
            skCircle(sketch, "E648", {"center": v(44086.3, 57596.56) * mm, "radius": 300 * mm});
            skCircle(sketch, "E649", {"center": v(42647.96, 57161.2) * mm, "radius": 300 * mm});
            skCircle(sketch, "E650", {"center": v(43367, 57378.84) * mm, "radius": 300 * mm});
            skCircle(sketch, "E651", {"center": v(33483.8, 61505.57) * mm, "radius": 300 * mm});
            skLineSegment(sketch, "E652", {"start": v(40350.08, 52642.78) * mm, "end": v(39290.08, 56144.84) * mm});
            skLineSegment(sketch, "E653", {"start": v(36517.3, 51483.84) * mm, "end": v(35457.62, 54984.83) * mm});
            skCircle(sketch, "E654", {"center": v(33621.22, 60726.77) * mm, "radius": 375 * mm});
            skLineSegment(sketch, "E655", {"start": v(35123.8, 56106.32) * mm, "end": v(35600.08, 54499.8) * mm});
            skLineSegment(sketch, "E656", {"start": v(34931.23, 56052.24) * mm, "end": v(35408.33, 54442.95) * mm});
            skLineSegment(sketch, "E657", {"start": v(34713.87, 57650.93) * mm, "end": v(35123.8, 56106.32) * mm});
            skLineSegment(sketch, "E658", {"start": v(34522.07, 57593.97) * mm, "end": v(34931.23, 56052.24) * mm});
            skLineSegment(sketch, "E659", {"start": v(34069.7, 59608.22) * mm, "end": v(34713.87, 57650.93) * mm});
            skLineSegment(sketch, "E660", {"start": v(33879.73, 59545.7) * mm, "end": v(34522.07, 57593.97) * mm});
            skLineSegment(sketch, "E661", {"start": v(33879.73, 59545.7) * mm, "end": v(34069.7, 59608.22) * mm});
            skCircle(sketch, "E662", {"center": v(35503.23, 54471.13) * mm, "radius": 375 * mm});
            skCircle(sketch, "E663", {"center": v(35024.65, 56078.4) * mm, "radius": 375 * mm});
            skCircle(sketch, "E664", {"center": v(34617.97, 57622.45) * mm, "radius": 300 * mm});
            skCircle(sketch, "E665", {"center": v(33974.72, 59576.96) * mm, "radius": 375 * mm});
            skCircle(sketch, "E666", {"center": v(35948.4, 52971.91) * mm, "radius": 375 * mm});
            skCircle(sketch, "E667", {"center": v(36387.31, 51517) * mm, "radius": 375 * mm});
            skCircle(sketch, "E668", {"center": v(37796.6, 51792.76) * mm, "radius": 375 * mm});
            skCircle(sketch, "E669", {"center": v(39835.27, 56332.54) * mm, "radius": 375 * mm});
            skCircle(sketch, "E670", {"center": v(41846.6, 56950.07) * mm, "radius": 375 * mm});
            skLineSegment(sketch, "E671", {"start": v(35706.21, 54140.42) * mm, "end": v(35937.9, 53360.17) * mm});
            skLineSegment(sketch, "E672", {"start": v(35746.17, 53303.24) * mm, "end": v(35937.9, 53360.17) * mm});
            skLineSegment(sketch, "E673", {"start": v(35514.49, 54083.49) * mm, "end": v(35746.17, 53303.24) * mm});
            skLineSegment(sketch, "E674", {"start": v(35514.49, 54083.49) * mm, "end": v(35706.21, 54140.42) * mm});
            skLineSegment(sketch, "E675", {"start": v(36152.82, 52642.08) * mm, "end": v(36375.12, 51905.21) * mm});
            skLineSegment(sketch, "E676", {"start": v(36183.64, 51847.45) * mm, "end": v(36375.12, 51905.21) * mm});
            skLineSegment(sketch, "E677", {"start": v(35961.34, 52584.32) * mm, "end": v(36183.64, 51847.45) * mm});
            skLineSegment(sketch, "E678", {"start": v(35961.34, 52584.32) * mm, "end": v(36152.82, 52642.08) * mm});
            skLineSegment(sketch, "E679", {"start": v(36736.53, 51687.4) * mm, "end": v(37409.39, 51818.95) * mm});
            skLineSegment(sketch, "E680", {"start": v(37447.76, 51622.67) * mm, "end": v(37409.39, 51818.95) * mm});
            skLineSegment(sketch, "E681", {"start": v(36774.9, 51491.12) * mm, "end": v(37447.76, 51622.67) * mm});
            skLineSegment(sketch, "E682", {"start": v(36774.9, 51491.12) * mm, "end": v(36736.53, 51687.4) * mm});
            skLineSegment(sketch, "E683", {"start": v(40164.4, 56538.2) * mm, "end": v(41458.77, 56935.6) * mm});
            skLineSegment(sketch, "E684", {"start": v(41517.47, 56744.4) * mm, "end": v(41458.77, 56935.6) * mm});
            skLineSegment(sketch, "E685", {"start": v(40223.1, 56347) * mm, "end": v(41517.47, 56744.4) * mm});
            skLineSegment(sketch, "E686", {"start": v(40223.1, 56347) * mm, "end": v(40164.4, 56538.2) * mm});
            skCircle(sketch, "E687", {"center": v(38530.81, 52093.36) * mm, "radius": 300 * mm});
            skCircle(sketch, "E688", {"center": v(39248.7, 52310.48) * mm, "radius": 300 * mm});
            skCircle(sketch, "E689", {"center": v(39966.5, 52527.84) * mm, "radius": 300 * mm});
            skLineSegment(sketch, "E690", {"start": v(36517.4, 51483.94) * mm, "end": v(40348.6, 52643.57) * mm});
            skLineSegment(sketch, "E691", {"start": v(39290.08, 56144.84) * mm, "end": v(44398.2, 57690.92) * mm});
            skCircle(sketch, "E692", {"center": v(67171.9, 49625.85) * mm, "radius": 300 * mm});
            skLineSegment(sketch, "E693", {"start": v(43459.74, 61481.43) * mm, "end": v(43746.88, 61568.34) * mm});
            skLineSegment(sketch, "E694", {"start": v(43746.88, 61568.34) * mm, "end": v(43833.79, 61281.2) * mm});
            skLineSegment(sketch, "E695", {"start": v(43833.79, 61281.2) * mm, "end": v(43546.65, 61194.3) * mm});
            skLineSegment(sketch, "E696", {"start": v(43546.65, 61194.3) * mm, "end": v(43459.74, 61481.43) * mm});
            skLineSegment(sketch, "E697", {"start": v(43546.65, 61194.3) * mm, "end": v(43824.77, 60275.46) * mm});
            skLineSegment(sketch, "E698", {"start": v(43833.79, 61281.2) * mm, "end": v(44112, 60362.4) * mm});
            skLineSegment(sketch, "E699", {"start": v(49601.8, 74661.76) * mm, "end": v(50131.26, 70514.15) * mm});
            skLineSegment(sketch, "E700", {"start": v(49304.21, 74623.77) * mm, "end": v(49909.66, 69880.9) * mm});
            skLineSegment(sketch, "E701", {"start": v(49304.21, 74623.77) * mm, "end": v(49601.8, 74661.76) * mm});
            skLineSegment(sketch, "E702", {"start": v(47015.81, 71647.18) * mm, "end": v(47180.44, 70357.55) * mm});
            skLineSegment(sketch, "E703", {"start": v(46882.85, 70319.56) * mm, "end": v(47180.44, 70357.55) * mm});
            skLineSegment(sketch, "E704", {"start": v(46718.23, 71609.2) * mm, "end": v(46882.85, 70319.56) * mm});
            skLineSegment(sketch, "E705", {"start": v(46718.23, 71609.2) * mm, "end": v(47015.81, 71647.18) * mm});
            skLineSegment(sketch, "E706", {"start": v(41460.6, 70937.97) * mm, "end": v(41625.98, 69648.52) * mm});
            skLineSegment(sketch, "E707", {"start": v(41328.42, 69610.36) * mm, "end": v(41625.98, 69648.52) * mm});
            skLineSegment(sketch, "E708", {"start": v(41163.04, 70899.8) * mm, "end": v(41328.42, 69610.36) * mm});
            skLineSegment(sketch, "E709", {"start": v(41163.04, 70899.8) * mm, "end": v(41460.6, 70937.97) * mm});
            skLineSegment(sketch, "E710", {"start": v(38209.1, 59892.17) * mm, "end": v(43746.98, 61568.38) * mm});
            skLineSegment(sketch, "E711", {"start": v(42856.08, 61298.72) * mm, "end": v(43746.98, 61568.38) * mm});
            skLineSegment(sketch, "E712", {"start": v(38296.02, 59605.04) * mm, "end": v(43833.9, 61281.24) * mm});
            skLineSegment(sketch, "E713", {"start": v(38209.1, 59892.17) * mm, "end": v(42377.52, 61153.87) * mm});
            skLineSegment(sketch, "E714", {"start": v(37749.93, 61409.25) * mm, "end": v(39136.07, 56829.58) * mm});
            skLineSegment(sketch, "E715", {"start": v(38296.02, 59605.04) * mm, "end": v(39136.07, 56829.58) * mm});
            skLineSegment(sketch, "E716", {"start": v(37462.8, 61322.34) * mm, "end": v(38848.93, 56742.67) * mm});
            skLineSegment(sketch, "E717", {"start": v(37749.93, 61409.25) * mm, "end": v(38209.1, 59892.17) * mm});
            skLineSegment(sketch, "E718", {"start": v(56060.35, 60596.37) * mm, "end": v(56498.65, 59810.3) * mm});
            skLineSegment(sketch, "E719", {"start": v(56192.96, 59639.86) * mm, "end": v(56498.65, 59810.3) * mm});
            skLineSegment(sketch, "E720", {"start": v(55754.66, 60425.92) * mm, "end": v(56192.96, 59639.86) * mm});
            skLineSegment(sketch, "E721", {"start": v(55754.66, 60425.92) * mm, "end": v(56060.35, 60596.37) * mm});
            skLineSegment(sketch, "E722", {"start": v(43746.88, 61568.34) * mm, "end": v(43459.74, 61481.43) * mm});
            skLineSegment(sketch, "E723", {"start": v(43833.79, 61281.2) * mm, "end": v(43746.88, 61568.34) * mm});
            skLineSegment(sketch, "E724", {"start": v(44643.83, 60262.21) * mm, "end": v(44184.42, 60123.16) * mm});
            skLineSegment(sketch, "E725", {"start": v(44571.41, 60501.5) * mm, "end": v(43824.87, 60275.54) * mm});
            skLineSegment(sketch, "E726", {"start": v(46706.45, 60886.5) * mm, "end": v(45505.24, 60522.94) * mm});
            skLineSegment(sketch, "E727", {"start": v(46634.03, 61125.79) * mm, "end": v(45432.82, 60762.22) * mm});
            skLineSegment(sketch, "E728", {"start": v(48505.84, 61431.13) * mm, "end": v(47759.29, 61205.17) * mm});
            skLineSegment(sketch, "E729", {"start": v(48672.7, 61742.83) * mm, "end": v(47686.86, 61444.45) * mm});
            skLineSegment(sketch, "E730", {"start": v(45469.03, 60642.58) * mm, "end": v(45505.24, 60522.94) * mm});
            skLineSegment(sketch, "E731", {"start": v(44607.62, 60381.85) * mm, "end": v(44643.83, 60262.21) * mm});
            skLineSegment(sketch, "E732", {"start": v(45469.03, 60642.58) * mm, "end": v(45432.82, 60762.22) * mm});
            skLineSegment(sketch, "E733", {"start": v(44607.62, 60381.85) * mm, "end": v(44571.41, 60501.5) * mm});
            skLineSegment(sketch, "E734", {"start": v(44571.41, 60501.5) * mm, "end": v(45432.82, 60762.22) * mm});
            skLineSegment(sketch, "E735", {"start": v(44643.83, 60262.21) * mm, "end": v(45505.24, 60522.94) * mm});
            skLineSegment(sketch, "E736", {"start": v(47723.07, 61324.8) * mm, "end": v(47759.29, 61205.17) * mm});
            skLineSegment(sketch, "E737", {"start": v(46670.24, 61006.15) * mm, "end": v(46706.45, 60886.5) * mm});
            skLineSegment(sketch, "E738", {"start": v(47723.07, 61324.8) * mm, "end": v(47686.86, 61444.45) * mm});
            skLineSegment(sketch, "E739", {"start": v(46670.24, 61006.15) * mm, "end": v(46634.03, 61125.79) * mm});
            skLineSegment(sketch, "E740", {"start": v(46634.03, 61125.79) * mm, "end": v(47686.86, 61444.45) * mm});
            skLineSegment(sketch, "E741", {"start": v(46706.45, 60886.5) * mm, "end": v(47759.29, 61205.17) * mm});
            skLineSegment(sketch, "E742", {"start": v(48672.7, 61742.83) * mm, "end": v(49476.62, 59086.75) * mm});
            skLineSegment(sketch, "E743", {"start": v(48505.84, 61431.13) * mm, "end": v(49091.04, 59497.67) * mm});
            skLineSegment(sketch, "E744", {"start": v(44184.42, 60123.16) * mm, "end": v(44769.56, 58189.64) * mm});
            skLineSegment(sketch, "E745", {"start": v(43824.87, 60275.54) * mm, "end": v(44628.7, 57619.38) * mm});
            skLineSegment(sketch, "E746", {"start": v(46549.88, 58728.5) * mm, "end": v(45964.7, 60661.96) * mm});
            skLineSegment(sketch, "E747", {"start": v(46741.3, 58786.45) * mm, "end": v(46156.12, 60719.9) * mm});
            skLineSegment(sketch, "E748", {"start": v(49726, 58953.22) * mm, "end": v(44495.31, 57370.09) * mm});
            skLineSegment(sketch, "E749", {"start": v(49476.63, 59086.71) * mm, "end": v(44628.8, 57619.45) * mm});
            skLineSegment(sketch, "E750", {"start": v(49476.62, 59086.75) * mm, "end": v(44628.7, 57619.38) * mm});
            skLineSegment(sketch, "E751", {"start": v(49091.04, 59497.67) * mm, "end": v(46741.3, 58786.45) * mm});
            skLineSegment(sketch, "E752", {"start": v(44495.31, 57370.09) * mm, "end": v(44311.28, 57978.1) * mm});
            skLineSegment(sketch, "E753", {"start": v(44502.7, 58036.03) * mm, "end": v(44311.28, 57978.1) * mm});
            skLineSegment(sketch, "E754", {"start": v(44628.8, 57619.45) * mm, "end": v(44502.7, 58036.03) * mm});
            skLineSegment(sketch, "E755", {"start": v(60131.76, 53293.71) * mm, "end": v(60570.05, 52507.65) * mm});
            skLineSegment(sketch, "E756", {"start": v(60264.36, 52337.2) * mm, "end": v(60570.05, 52507.65) * mm});
            skLineSegment(sketch, "E757", {"start": v(59826.06, 53123.27) * mm, "end": v(60264.36, 52337.2) * mm});
            skLineSegment(sketch, "E758", {"start": v(59826.06, 53123.27) * mm, "end": v(60131.76, 53293.71) * mm});
            skLineSegment(sketch, "E759", {"start": v(47885.55, 61765.78) * mm, "end": v(48364.1, 61910.63) * mm});
            skLineSegment(sketch, "E760", {"start": v(47957.97, 61526.5) * mm, "end": v(48436.53, 61671.35) * mm});
            skLineSegment(sketch, "E761", {"start": v(47957.97, 61526.5) * mm, "end": v(47885.55, 61765.78) * mm});
            skLineSegment(sketch, "E762", {"start": v(34583.64, 74073.32) * mm, "end": v(34277.71, 74103.31) * mm});
            skLineSegment(sketch, "E763", {"start": v(36509.2, 74336.72) * mm, "end": v(36210.42, 74264.44) * mm});
            skLineSegment(sketch, "E764", {"start": v(38568.06, 74568.37) * mm, "end": v(38260.66, 74568.37) * mm});
            skLineSegment(sketch, "E765", {"start": v(40630.85, 74832.8) * mm, "end": v(40326.88, 74787.02) * mm});
            skLineSegment(sketch, "E766", {"start": v(42529.89, 75035.76) * mm, "end": v(42224.21, 75003.22) * mm});
            skLineSegment(sketch, "E767", {"start": v(44620.7, 75346.4) * mm, "end": v(44315.83, 75306.98) * mm});
            skLineSegment(sketch, "E768", {"start": v(46260.89, 75467.94) * mm, "end": v(45954.04, 75449.5) * mm});
            skLineSegment(sketch, "E769", {"start": v(48411.94, 75732.02) * mm, "end": v(48106.56, 75696.83) * mm});
            skLineSegment(sketch, "E770", {"start": v(34308.4, 74416.31) * mm, "end": v(34614.33, 74386.32) * mm});
            skLineSegment(sketch, "E771", {"start": v(34306.57, 74397.7) * mm, "end": v(34612.5, 74367.7) * mm});
            skLineSegment(sketch, "E772", {"start": v(34614.33, 74386.32) * mm, "end": v(34612.5, 74367.7) * mm});
            skLineSegment(sketch, "E773", {"start": v(34585.47, 74091.93) * mm, "end": v(34583.64, 74073.32) * mm});
            skLineSegment(sketch, "E774", {"start": v(34585.47, 74091.93) * mm, "end": v(34279.53, 74121.92) * mm});
            skLineSegment(sketch, "E775", {"start": v(34277.71, 74103.31) * mm, "end": v(34279.53, 74121.92) * mm});
            skLineSegment(sketch, "E776", {"start": v(34306.57, 74397.7) * mm, "end": v(34308.4, 74416.31) * mm});
            skLineSegment(sketch, "E777", {"start": v(34465.5, 74382.12) * mm, "end": v(34438.47, 74106.34) * mm});
            skLineSegment(sketch, "E778", {"start": v(34453.57, 74383.29) * mm, "end": v(34426.53, 74107.51) * mm});
            skLineSegment(sketch, "E779", {"start": v(36136.47, 74570.12) * mm, "end": v(36435.25, 74642.4) * mm});
            skLineSegment(sketch, "E780", {"start": v(36140.87, 74551.95) * mm, "end": v(36439.65, 74624.22) * mm});
            skLineSegment(sketch, "E781", {"start": v(36435.25, 74642.4) * mm, "end": v(36439.65, 74624.22) * mm});
            skLineSegment(sketch, "E782", {"start": v(36504.8, 74354.9) * mm, "end": v(36509.2, 74336.72) * mm});
            skLineSegment(sketch, "E783", {"start": v(36504.8, 74354.9) * mm, "end": v(36206.02, 74282.62) * mm});
            skLineSegment(sketch, "E784", {"start": v(36210.42, 74264.44) * mm, "end": v(36206.02, 74282.62) * mm});
            skLineSegment(sketch, "E785", {"start": v(36140.87, 74551.95) * mm, "end": v(36136.47, 74570.12) * mm});
            skLineSegment(sketch, "E786", {"start": v(36296.1, 74589.5) * mm, "end": v(36361.24, 74320.16) * mm});
            skLineSegment(sketch, "E787", {"start": v(36284.43, 74586.68) * mm, "end": v(36349.58, 74317.34) * mm});
            skLineSegment(sketch, "E788", {"start": v(38260.66, 74882.87) * mm, "end": v(38568.06, 74882.87) * mm});
            skLineSegment(sketch, "E789", {"start": v(38260.66, 74864.17) * mm, "end": v(38568.06, 74864.17) * mm});
            skLineSegment(sketch, "E790", {"start": v(38568.06, 74882.87) * mm, "end": v(38568.06, 74864.17) * mm});
            skLineSegment(sketch, "E791", {"start": v(38568.06, 74587.07) * mm, "end": v(38568.06, 74568.37) * mm});
            skLineSegment(sketch, "E792", {"start": v(38568.06, 74587.07) * mm, "end": v(38260.66, 74587.07) * mm});
            skLineSegment(sketch, "E793", {"start": v(38260.66, 74568.37) * mm, "end": v(38260.66, 74587.07) * mm});
            skLineSegment(sketch, "E794", {"start": v(38260.66, 74864.17) * mm, "end": v(38260.66, 74882.87) * mm});
            skLineSegment(sketch, "E795", {"start": v(38420.36, 74864.17) * mm, "end": v(38420.36, 74587.07) * mm});
            skLineSegment(sketch, "E796", {"start": v(38408.36, 74864.17) * mm, "end": v(38408.36, 74587.07) * mm});
            skLineSegment(sketch, "E797", {"start": v(40280.05, 75098.01) * mm, "end": v(40584.02, 75143.79) * mm});
            skLineSegment(sketch, "E798", {"start": v(40282.83, 75079.52) * mm, "end": v(40586.8, 75125.3) * mm});
            skLineSegment(sketch, "E799", {"start": v(40584.02, 75143.79) * mm, "end": v(40586.8, 75125.3) * mm});
            skLineSegment(sketch, "E800", {"start": v(40628.07, 74851.29) * mm, "end": v(40630.85, 74832.8) * mm});
            skLineSegment(sketch, "E801", {"start": v(40628.07, 74851.29) * mm, "end": v(40324.1, 74805.5) * mm});
            skLineSegment(sketch, "E802", {"start": v(40326.88, 74787.02) * mm, "end": v(40324.1, 74805.5) * mm});
            skLineSegment(sketch, "E803", {"start": v(40282.83, 75079.52) * mm, "end": v(40280.05, 75098.01) * mm});
            skLineSegment(sketch, "E804", {"start": v(40440.75, 75103.3) * mm, "end": v(40482.02, 74829.3) * mm});
            skLineSegment(sketch, "E805", {"start": v(40428.89, 75101.51) * mm, "end": v(40470.15, 74827.5) * mm});
            skLineSegment(sketch, "E806", {"start": v(42190.92, 75315.95) * mm, "end": v(42496.6, 75348.5) * mm});
            skLineSegment(sketch, "E807", {"start": v(42192.9, 75297.36) * mm, "end": v(42498.58, 75329.9) * mm});
            skLineSegment(sketch, "E808", {"start": v(42496.6, 75348.5) * mm, "end": v(42498.58, 75329.9) * mm});
            skLineSegment(sketch, "E809", {"start": v(42527.9, 75054.35) * mm, "end": v(42529.89, 75035.76) * mm});
            skLineSegment(sketch, "E810", {"start": v(42527.9, 75054.35) * mm, "end": v(42222.24, 75021.82) * mm});
            skLineSegment(sketch, "E811", {"start": v(42224.21, 75003.22) * mm, "end": v(42222.24, 75021.82) * mm});
            skLineSegment(sketch, "E812", {"start": v(42192.9, 75297.36) * mm, "end": v(42190.92, 75315.95) * mm});
            skLineSegment(sketch, "E813", {"start": v(42351.7, 75314.26) * mm, "end": v(42381.04, 75038.72) * mm});
            skLineSegment(sketch, "E814", {"start": v(42339.77, 75313) * mm, "end": v(42369.1, 75037.45) * mm});
            skLineSegment(sketch, "E815", {"start": v(44275.5, 75618.88) * mm, "end": v(44580.37, 75658.3) * mm});
            skLineSegment(sketch, "E816", {"start": v(44277.9, 75600.34) * mm, "end": v(44582.77, 75639.76) * mm});
            skLineSegment(sketch, "E817", {"start": v(44580.37, 75658.3) * mm, "end": v(44582.77, 75639.76) * mm});
            skLineSegment(sketch, "E818", {"start": v(44618.3, 75364.94) * mm, "end": v(44620.7, 75346.4) * mm});
            skLineSegment(sketch, "E819", {"start": v(44618.3, 75364.94) * mm, "end": v(44313.44, 75325.53) * mm});
            skLineSegment(sketch, "E820", {"start": v(44315.83, 75306.98) * mm, "end": v(44313.44, 75325.53) * mm});
            skLineSegment(sketch, "E821", {"start": v(44277.9, 75600.34) * mm, "end": v(44275.5, 75618.88) * mm});
            skLineSegment(sketch, "E822", {"start": v(44436.28, 75620.82) * mm, "end": v(44471.82, 75346) * mm});
            skLineSegment(sketch, "E823", {"start": v(44424.38, 75619.28) * mm, "end": v(44459.92, 75344.46) * mm});
            skLineSegment(sketch, "E824", {"start": v(45935.18, 75763.44) * mm, "end": v(46242.02, 75781.88) * mm});
            skLineSegment(sketch, "E825", {"start": v(45936.3, 75744.77) * mm, "end": v(46243.14, 75763.21) * mm});
            skLineSegment(sketch, "E826", {"start": v(46242.02, 75781.88) * mm, "end": v(46243.14, 75763.21) * mm});
            skLineSegment(sketch, "E827", {"start": v(46259.76, 75486.61) * mm, "end": v(46260.89, 75467.94) * mm});
            skLineSegment(sketch, "E828", {"start": v(46259.76, 75486.61) * mm, "end": v(45952.92, 75468.17) * mm});
            skLineSegment(sketch, "E829", {"start": v(45954.04, 75449.5) * mm, "end": v(45952.92, 75468.17) * mm});
            skLineSegment(sketch, "E830", {"start": v(45936.3, 75744.77) * mm, "end": v(45935.18, 75763.44) * mm});
            skLineSegment(sketch, "E831", {"start": v(46095.71, 75754.35) * mm, "end": v(46112.33, 75477.75) * mm});
            skLineSegment(sketch, "E832", {"start": v(46083.73, 75753.63) * mm, "end": v(46100.35, 75477.03) * mm});
            skLineSegment(sketch, "E833", {"start": v(48070.56, 76009.27) * mm, "end": v(48375.94, 76044.45) * mm});
            skLineSegment(sketch, "E834", {"start": v(48072.7, 75990.69) * mm, "end": v(48378.08, 76025.87) * mm});
            skLineSegment(sketch, "E835", {"start": v(48375.94, 76044.45) * mm, "end": v(48378.08, 76025.87) * mm});
            skLineSegment(sketch, "E836", {"start": v(48409.8, 75750.6) * mm, "end": v(48411.94, 75732.02) * mm});
            skLineSegment(sketch, "E837", {"start": v(48409.8, 75750.6) * mm, "end": v(48104.42, 75715.4) * mm});
            skLineSegment(sketch, "E838", {"start": v(48106.56, 75696.83) * mm, "end": v(48104.42, 75715.4) * mm});
            skLineSegment(sketch, "E839", {"start": v(48072.7, 75990.69) * mm, "end": v(48070.56, 76009.27) * mm});
            skLineSegment(sketch, "E840", {"start": v(48231.35, 76008.97) * mm, "end": v(48263.07, 75733.69) * mm});
            skLineSegment(sketch, "E841", {"start": v(48219.43, 76007.6) * mm, "end": v(48251.15, 75732.31) * mm});
            skLineSegment(sketch, "E842", {"start": v(34452, 74244.23) * mm, "end": v(34440.05, 74245.4) * mm});
            skLineSegment(sketch, "E843", {"start": v(36328.67, 74454.83) * mm, "end": v(36317, 74452) * mm});
            skLineSegment(sketch, "E844", {"start": v(38420.36, 74725.62) * mm, "end": v(38408.36, 74725.62) * mm});
            skLineSegment(sketch, "E845", {"start": v(40461.39, 74966.3) * mm, "end": v(40449.52, 74964.5) * mm});
            skLineSegment(sketch, "E846", {"start": v(42366.37, 75176.5) * mm, "end": v(42354.44, 75175.22) * mm});
            skLineSegment(sketch, "E847", {"start": v(44454.05, 75483.4) * mm, "end": v(44442.15, 75481.87) * mm});
            skLineSegment(sketch, "E848", {"start": v(46104.02, 75616.05) * mm, "end": v(46092.04, 75615.33) * mm});
            skLineSegment(sketch, "E849", {"start": v(48247.21, 75871.33) * mm, "end": v(48235.3, 75869.95) * mm});
            skCircle(sketch, "E850", {"center": v(34446.02, 74244.82) * mm, "radius": 300 * mm});
            skCircle(sketch, "E851", {"center": v(36322.84, 74453.42) * mm, "radius": 300 * mm});
            skCircle(sketch, "E852", {"center": v(38414.36, 74725.62) * mm, "radius": 300 * mm});
            skCircle(sketch, "E853", {"center": v(40455.45, 74965.4) * mm, "radius": 300 * mm});
            skCircle(sketch, "E854", {"center": v(42360.4, 75175.86) * mm, "radius": 300 * mm});
            skCircle(sketch, "E855", {"center": v(44448.1, 75482.64) * mm, "radius": 300 * mm});
            skCircle(sketch, "E856", {"center": v(46098.03, 75615.7) * mm, "radius": 300 * mm});
            skCircle(sketch, "E857", {"center": v(48241.25, 75870.64) * mm, "radius": 300 * mm});
            skCircle(sketch, "E858", {"center": v(34776.7, 58413.82) * mm, "radius": 328.69 * mm});
            skCircle(sketch, "E859", {"center": v(35224.5, 57091.4) * mm, "radius": 323.11 * mm});
            skCircle(sketch, "E860", {"center": v(35826.9, 55480) * mm, "radius": 308.82 * mm});
            skCircle(sketch, "E861", {"center": v(36309.94, 53902.1) * mm, "radius": 312.62 * mm});
            skCircle(sketch, "E862", {"center": v(36823.57, 52431.1) * mm, "radius": 314.17 * mm});
            skCircle(sketch, "E863", {"center": v(37258.05, 50987.66) * mm, "radius": 280.53 * mm});
            skLineSegment(sketch, "E864", {"start": v(44215.6, 60106.43) * mm, "end": v(45947.99, 60630.79) * mm});
            skLineSegment(sketch, "E865", {"start": v(45947.99, 60630.79) * mm, "end": v(46469.45, 58907.97) * mm});
            skLineSegment(sketch, "E866", {"start": v(46469.45, 58907.97) * mm, "end": v(44737.06, 58383.62) * mm});
            skLineSegment(sketch, "E867", {"start": v(44737.06, 58383.62) * mm, "end": v(44215.6, 60106.43) * mm});
            skLineSegment(sketch, "E868", {"start": v(44643.85, 60262.18) * mm, "end": v(45505.25, 60522.9) * mm});
            skLineSegment(sketch, "E869", {"start": v(49476.63, 59086.71) * mm, "end": v(49350.51, 59503.37) * mm});
            skLineSegment(sketch, "E870", {"start": v(49726, 58953.22) * mm, "end": v(49541.94, 59561.3) * mm});
            skLineSegment(sketch, "E871", {"start": v(51278.99, 57177.09) * mm, "end": v(56516.32, 58762.32) * mm});
            skLineSegment(sketch, "E872", {"start": v(56665.85, 58494.14) * mm, "end": v(51365.9, 56889.95) * mm});
            skLineSegment(sketch, "E873", {"start": v(50131.26, 70514.15) * mm, "end": v(50593.39, 70573.29) * mm});
            skLineSegment(sketch, "E874", {"start": v(50669.54, 69978.14) * mm, "end": v(50593.39, 70573.29) * mm});
            skLineSegment(sketch, "E875", {"start": v(49909.66, 69880.9) * mm, "end": v(50669.54, 69978.14) * mm});
            skLineSegment(sketch, "E876", {"start": v(47841.4, 61911.65) * mm, "end": v(48319.95, 62056.5) * mm});
            skLineSegment(sketch, "E877", {"start": v(48392.38, 61817.22) * mm, "end": v(48319.95, 62056.5) * mm});
            skLineSegment(sketch, "E878", {"start": v(47913.82, 61672.37) * mm, "end": v(48392.38, 61817.22) * mm});
            skLineSegment(sketch, "E879", {"start": v(47913.82, 61672.37) * mm, "end": v(47841.4, 61911.65) * mm});
            skLineSegment(sketch, "E880", {"start": v(58318.92, 63332.61) * mm, "end": v(58586.76, 62852.24) * mm});
            skLineSegment(sketch, "E881", {"start": v(58368.41, 62730.5) * mm, "end": v(58586.76, 62852.24) * mm});
            skLineSegment(sketch, "E882", {"start": v(58100.57, 63210.86) * mm, "end": v(58368.41, 62730.5) * mm});
            skLineSegment(sketch, "E883", {"start": v(58100.57, 63210.86) * mm, "end": v(58318.92, 63332.61) * mm});
            skLineSegment(sketch, "E884", {"start": v(59393.32, 61405.46) * mm, "end": v(59661.17, 60925.09) * mm});
            skLineSegment(sketch, "E885", {"start": v(59442.82, 60803.34) * mm, "end": v(59661.17, 60925.09) * mm});
            skLineSegment(sketch, "E886", {"start": v(59174.97, 61283.7) * mm, "end": v(59442.82, 60803.34) * mm});
            skLineSegment(sketch, "E887", {"start": v(59174.97, 61283.7) * mm, "end": v(59393.32, 61405.46) * mm});
            skLineSegment(sketch, "E888", {"start": v(61824.92, 57043.9) * mm, "end": v(62092.77, 56563.53) * mm});
            skLineSegment(sketch, "E889", {"start": v(61874.42, 56441.78) * mm, "end": v(62092.77, 56563.53) * mm});
            skLineSegment(sketch, "E890", {"start": v(61606.57, 56922.15) * mm, "end": v(61874.42, 56441.78) * mm});
            skLineSegment(sketch, "E891", {"start": v(61606.57, 56922.15) * mm, "end": v(61824.92, 57043.9) * mm});
            skLineSegment(sketch, "E892", {"start": v(62899.33, 55116.74) * mm, "end": v(63167.18, 54636.37) * mm});
            skLineSegment(sketch, "E893", {"start": v(62948.82, 54514.62) * mm, "end": v(63167.18, 54636.37) * mm});
            skLineSegment(sketch, "E894", {"start": v(62680.98, 54995) * mm, "end": v(62948.82, 54514.62) * mm});
            skLineSegment(sketch, "E895", {"start": v(62680.98, 54995) * mm, "end": v(62899.33, 55116.74) * mm});
            skLineSegment(sketch, "E896", {"start": v(55887.31, 67694.17) * mm, "end": v(56155.16, 67213.8) * mm});
            skLineSegment(sketch, "E897", {"start": v(55936.81, 67092.05) * mm, "end": v(56155.16, 67213.8) * mm});
            skLineSegment(sketch, "E898", {"start": v(55668.96, 67572.42) * mm, "end": v(55936.81, 67092.05) * mm});
            skLineSegment(sketch, "E899", {"start": v(55668.96, 67572.42) * mm, "end": v(55887.31, 67694.17) * mm});
            skLineSegment(sketch, "E900", {"start": v(54812.9, 69621.33) * mm, "end": v(55080.76, 69140.96) * mm});
            skLineSegment(sketch, "E901", {"start": v(54862.4, 69019.2) * mm, "end": v(55080.76, 69140.96) * mm});
            skLineSegment(sketch, "E902", {"start": v(54594.56, 69499.58) * mm, "end": v(54862.4, 69019.2) * mm});
            skLineSegment(sketch, "E903", {"start": v(54594.56, 69499.58) * mm, "end": v(54812.9, 69621.33) * mm});
            skLineSegment(sketch, "E904", {"start": v(56155.16, 67213.8) * mm, "end": v(55936.81, 67092.05) * mm});
            skLineSegment(sketch, "E905", {"start": v(55936.81, 67092.05) * mm, "end": v(55668.96, 67572.42) * mm});
            skLineSegment(sketch, "E906", {"start": v(57613.6, 55160.75) * mm, "end": v(58392.95, 55396.7) * mm});
            skLineSegment(sketch, "E907", {"start": v(59038.3, 52605.67) * mm, "end": v(59817.63, 52841.6) * mm});
            skLineSegment(sketch, "E908", {"start": v(52375.25, 73993.75) * mm, "end": v(52643.1, 73513.38) * mm});
            skLineSegment(sketch, "E909", {"start": v(52424.75, 73391.63) * mm, "end": v(52643.1, 73513.38) * mm});
            skLineSegment(sketch, "E910", {"start": v(52156.9, 73872) * mm, "end": v(52424.75, 73391.63) * mm});
            skLineSegment(sketch, "E911", {"start": v(52156.9, 73872) * mm, "end": v(52375.25, 73993.75) * mm});
            skLineSegment(sketch, "E912", {"start": v(52281.23, 65747.36) * mm, "end": v(53057.73, 65982.39) * mm});
            skLineSegment(sketch, "E913", {"start": v(52418.84, 65292.73) * mm, "end": v(53000.6, 65468.81) * mm});
            skLineSegment(sketch, "E914", {"start": v(52418.84, 65292.73) * mm, "end": v(52281.23, 65747.36) * mm});
            skLineSegment(sketch, "E915", {"start": v(54045.3, 63436.93) * mm, "end": v(55287.74, 59332.08) * mm});
            skLineSegment(sketch, "E916", {"start": v(53758.17, 63350.02) * mm, "end": v(54874.02, 59663.37) * mm});
            skLineSegment(sketch, "E917", {"start": v(53380.3, 65116.29) * mm, "end": v(53523.86, 65159.74) * mm});
            skLineSegment(sketch, "E918", {"start": v(53901.74, 63393.47) * mm, "end": v(54045.3, 63436.93) * mm});
            skLineSegment(sketch, "E919", {"start": v(53380.3, 65116.29) * mm, "end": v(53236.72, 65072.83) * mm});
            skLineSegment(sketch, "E920", {"start": v(53901.74, 63393.47) * mm, "end": v(53758.17, 63350.02) * mm});
            skLineSegment(sketch, "E921", {"start": v(53758.17, 63350.02) * mm, "end": v(53236.72, 65072.83) * mm});
            skLineSegment(sketch, "E922", {"start": v(54045.3, 63436.93) * mm, "end": v(53523.86, 65159.74) * mm});
            skLineSegment(sketch, "E923", {"start": v(53236.72, 65072.83) * mm, "end": v(53758.17, 63350.02) * mm});
            skLineSegment(sketch, "E924", {"start": v(53523.86, 65159.74) * mm, "end": v(54045.3, 63436.93) * mm});
            skLineSegment(sketch, "E925", {"start": v(35194.47, 68817.29) * mm, "end": v(34817.9, 70061.55) * mm});
            skLineSegment(sketch, "E926", {"start": v(35105.03, 70148.46) * mm, "end": v(34817.9, 70061.55) * mm});
            skLineSegment(sketch, "E927", {"start": v(35481.6, 68904.2) * mm, "end": v(35105.03, 70148.46) * mm});
            skLineSegment(sketch, "E928", {"start": v(35481.6, 68904.2) * mm, "end": v(35194.47, 68817.29) * mm});
            skLineSegment(sketch, "E929", {"start": v(42377.52, 61153.87) * mm, "end": v(42261.62, 61536.8) * mm});
            skLineSegment(sketch, "E930", {"start": v(42740.18, 61681.65) * mm, "end": v(42261.62, 61536.8) * mm});
            skLineSegment(sketch, "E931", {"start": v(42856.08, 61298.72) * mm, "end": v(42740.18, 61681.65) * mm});
            skLineSegment(sketch, "E932", {"start": v(53225.02, 65066.3) * mm, "end": v(53000.6, 65468.81) * mm});
            skLineSegment(sketch, "E933", {"start": v(53487.04, 65212.4) * mm, "end": v(53057.73, 65982.39) * mm});
            skLineSegment(sketch, "E934", {"start": v(59287.5, 52158.7) * mm, "end": v(53342.63, 50359.31) * mm});
            skLineSegment(sketch, "E935", {"start": v(58991.9, 52278.2) * mm, "end": v(53284.69, 50550.73) * mm});
            skLineSegment(sketch, "E936", {"start": v(58991.9, 52278.2) * mm, "end": v(59187.82, 52337.5) * mm});
            skLineSegment(sketch, "E937", {"start": v(55287.74, 59332.08) * mm, "end": v(59187.82, 52337.5) * mm});
            skLineSegment(sketch, "E938", {"start": v(54874.02, 59663.37) * mm, "end": v(58991.9, 52278.2) * mm});
            skLineSegment(sketch, "E939", {"start": v(61463.3, 49888.88) * mm, "end": v(61702.18, 49961.19) * mm});
            skLineSegment(sketch, "E940", {"start": v(61702.18, 49961.19) * mm, "end": v(61774.6, 49721.9) * mm});
            skLineSegment(sketch, "E941", {"start": v(61774.6, 49721.9) * mm, "end": v(61535.73, 49649.6) * mm});
            skLineSegment(sketch, "E942", {"start": v(61535.73, 49649.6) * mm, "end": v(61463.3, 49888.88) * mm});
            skLineSegment(sketch, "E943", {"start": v(53291.1, 65935.67) * mm, "end": v(53529.97, 66007.97) * mm});
            skLineSegment(sketch, "E944", {"start": v(53529.97, 66007.97) * mm, "end": v(53602.4, 65768.7) * mm});
            skLineSegment(sketch, "E945", {"start": v(53602.4, 65768.7) * mm, "end": v(53363.52, 65696.4) * mm});
            skLineSegment(sketch, "E946", {"start": v(53363.52, 65696.4) * mm, "end": v(53291.1, 65935.67) * mm});
            skLineSegment(sketch, "E947", {"start": v(65900.3, 51172.38) * mm, "end": v(66118.29, 51293.9) * mm});
            skLineSegment(sketch, "E948", {"start": v(66118.29, 51293.9) * mm, "end": v(66240.02, 51075.55) * mm});
            skLineSegment(sketch, "E949", {"start": v(66240.02, 51075.55) * mm, "end": v(66022.03, 50954.02) * mm});
            skLineSegment(sketch, "E950", {"start": v(66022.03, 50954.02) * mm, "end": v(65900.3, 51172.38) * mm});
            skLineSegment(sketch, "E951", {"start": v(43166.65, 61878.55) * mm, "end": v(43405.52, 61950.85) * mm});
            skLineSegment(sketch, "E952", {"start": v(43405.52, 61950.85) * mm, "end": v(43477.94, 61711.57) * mm});
            skLineSegment(sketch, "E953", {"start": v(43477.94, 61711.57) * mm, "end": v(43239.07, 61639.27) * mm});
            skLineSegment(sketch, "E954", {"start": v(43239.07, 61639.27) * mm, "end": v(43166.65, 61878.55) * mm});
            skLineSegment(sketch, "E955", {"start": v(48366.02, 61911.21) * mm, "end": v(48604.9, 61983.51) * mm});
            skLineSegment(sketch, "E956", {"start": v(48604.9, 61983.51) * mm, "end": v(48677.32, 61744.23) * mm});
            skLineSegment(sketch, "E957", {"start": v(48677.32, 61744.23) * mm, "end": v(48438.45, 61671.93) * mm});
            skLineSegment(sketch, "E958", {"start": v(48438.45, 61671.93) * mm, "end": v(48366.02, 61911.21) * mm});
            skLineSegment(sketch, "E959", {"start": v(64065.34, 54464.23) * mm, "end": v(64283.47, 54585.5) * mm});
            skLineSegment(sketch, "E960", {"start": v(64283.47, 54585.5) * mm, "end": v(64404.95, 54367) * mm});
            skLineSegment(sketch, "E961", {"start": v(64404.95, 54367) * mm, "end": v(64186.82, 54245.73) * mm});
            skLineSegment(sketch, "E962", {"start": v(64186.82, 54245.73) * mm, "end": v(64065.34, 54464.23) * mm});
            skLineSegment(sketch, "E963", {"start": v(45953.73, 61181.06) * mm, "end": v(46192.6, 61253.36) * mm});
            skLineSegment(sketch, "E964", {"start": v(46192.6, 61253.36) * mm, "end": v(46265.03, 61014.08) * mm});
            skLineSegment(sketch, "E965", {"start": v(46265.03, 61014.08) * mm, "end": v(46026.16, 60941.78) * mm});
            skLineSegment(sketch, "E966", {"start": v(46026.16, 60941.78) * mm, "end": v(45953.73, 61181.06) * mm});
            skLineSegment(sketch, "E967", {"start": v(52418.02, 67337.58) * mm, "end": v(52656.9, 67409.89) * mm});
            skLineSegment(sketch, "E968", {"start": v(52656.9, 67409.89) * mm, "end": v(52729.32, 67170.6) * mm});
            skLineSegment(sketch, "E969", {"start": v(52729.32, 67170.6) * mm, "end": v(52490.45, 67098.3) * mm});
            skLineSegment(sketch, "E970", {"start": v(52490.45, 67098.3) * mm, "end": v(52418.02, 67337.58) * mm});
            skLineSegment(sketch, "E971", {"start": v(4.94, 5000) * mm, "end": v(0, -5000) * mm});
            skLineSegment(sketch, "E972", {"start": v(5000, 0) * mm, "end": v(-5000, -4.94) * mm});
            skCircle(sketch, "E973", {"center": v(0, -2.47) * mm, "radius": 1929.43 * mm});
            skLineSegment(sketch, "E974", {"start": v(58325.52, 53471.87) * mm, "end": v(58500.2, 53569.27) * mm});
            skLineSegment(sketch, "E975", {"start": v(58500.2, 53569.27) * mm, "end": v(58889.8, 52870.55) * mm});
            skLineSegment(sketch, "E976", {"start": v(58889.8, 52870.55) * mm, "end": v(58715.12, 52773.15) * mm});
            skLineSegment(sketch, "E977", {"start": v(58715.12, 52773.15) * mm, "end": v(58325.52, 53471.87) * mm});
            skLineSegment(sketch, "E978", {"start": v(32883.91, 66080.85) * mm, "end": v(33122.79, 66153.15) * mm});
            skLineSegment(sketch, "E979", {"start": v(33122.79, 66153.15) * mm, "end": v(33195.21, 65913.87) * mm});
            skLineSegment(sketch, "E980", {"start": v(33195.21, 65913.87) * mm, "end": v(32956.34, 65841.57) * mm});
            skLineSegment(sketch, "E981", {"start": v(32956.34, 65841.57) * mm, "end": v(32883.91, 66080.85) * mm});
            skLineSegment(sketch, "E982", {"start": v(32882.84, 66524.7) * mm, "end": v(32930.7, 66539.19) * mm});
            skLineSegment(sketch, "E983", {"start": v(44381.57, 66109.13) * mm, "end": v(46379.94, 66189.81) * mm});
            skLineSegment(sketch, "E984", {"start": v(46379.94, 66189.81) * mm, "end": v(46460.62, 64191.44) * mm});
            skLineSegment(sketch, "E985", {"start": v(46460.62, 64191.44) * mm, "end": v(44462.25, 64110.76) * mm});
            skLineSegment(sketch, "E986", {"start": v(44462.25, 64110.76) * mm, "end": v(44381.57, 66109.13) * mm});
            skLineSegment(sketch, "E987", {"start": v(44462.25, 64110.76) * mm, "end": v(46379.94, 66189.81) * mm});
            skLineSegment(sketch, "E988", {"start": v(44381.57, 66109.13) * mm, "end": v(46460.62, 64191.44) * mm});
            skCircle(sketch, "E989", {"center": v(42435, 71860) * mm, "radius": 350 * mm});
            skLineSegment(sketch, "E990", {"start": v(51034.44, 72929.32) * mm, "end": v(49850.78, 74290.55) * mm});
            skLineSegment(sketch, "E991", {"start": v(53640.78, 69956.14) * mm, "end": v(52836.54, 68341.45) * mm});
            skLineSegment(sketch, "E992", {"start": v(53830.5, 68468.18) * mm, "end": v(52646.83, 69829.4) * mm});
            skLineSegment(sketch, "E993", {"start": v(37274.9, 65820.2) * mm, "end": v(38473.93, 65868.61) * mm});
            skLineSegment(sketch, "E994", {"start": v(38473.93, 65868.61) * mm, "end": v(38510.16, 64971.35) * mm});
            skLineSegment(sketch, "E995", {"start": v(38510.16, 64971.35) * mm, "end": v(37311.13, 64922.95) * mm});
            skLineSegment(sketch, "E996", {"start": v(37311.13, 64922.95) * mm, "end": v(37274.9, 65820.2) * mm});
            skLineSegment(sketch, "E997", {"start": v(50791.39, 66363.5) * mm, "end": v(51990.41, 66411.9) * mm});
            skLineSegment(sketch, "E998", {"start": v(51990.41, 66411.9) * mm, "end": v(52026.64, 65514.65) * mm});
            skLineSegment(sketch, "E999", {"start": v(52026.64, 65514.65) * mm, "end": v(50827.61, 65466.24) * mm});
            skLineSegment(sketch, "E1000", {"start": v(50827.61, 65466.24) * mm, "end": v(50791.39, 66363.5) * mm});
            skLineSegment(sketch, "E1001", {"start": v(50791.39, 66363.5) * mm, "end": v(52026.64, 65514.65) * mm});
            skLineSegment(sketch, "E1002", {"start": v(51990.41, 66411.9) * mm, "end": v(50827.61, 65466.24) * mm});
            skLineSegment(sketch, "E1003", {"start": v(37311.13, 64922.95) * mm, "end": v(38473.93, 65868.61) * mm});
            skLineSegment(sketch, "E1004", {"start": v(38510.16, 64971.35) * mm, "end": v(37274.9, 65820.2) * mm});
            skLineSegment(sketch, "E1005", {"start": v(54534.84, 63584.32) * mm, "end": v(54187.28, 64732.89) * mm});
            skLineSegment(sketch, "E1006", {"start": v(54187.28, 64732.89) * mm, "end": v(55046.78, 64992.97) * mm});
            skLineSegment(sketch, "E1007", {"start": v(55046.78, 64992.97) * mm, "end": v(55394.34, 63844.4) * mm});
            skLineSegment(sketch, "E1008", {"start": v(55394.34, 63844.4) * mm, "end": v(54534.84, 63584.32) * mm});
            skLineSegment(sketch, "E1009", {"start": v(54534.84, 63584.32) * mm, "end": v(55046.78, 64992.97) * mm});
            skLineSegment(sketch, "E1010", {"start": v(54187.28, 64732.89) * mm, "end": v(55394.34, 63844.4) * mm});
            skLineSegment(sketch, "E1011", {"start": v(59168.74, 53933.32) * mm, "end": v(58821.16, 55081.88) * mm});
            skLineSegment(sketch, "E1012", {"start": v(58821.16, 55081.88) * mm, "end": v(59680.65, 55341.98) * mm});
            skLineSegment(sketch, "E1013", {"start": v(59680.65, 55341.98) * mm, "end": v(60028.23, 54193.42) * mm});
            skLineSegment(sketch, "E1014", {"start": v(60028.23, 54193.42) * mm, "end": v(59168.74, 53933.32) * mm});
            skLineSegment(sketch, "E1015", {"start": v(59168.74, 53933.32) * mm, "end": v(59680.65, 55341.98) * mm});
            skLineSegment(sketch, "E1016", {"start": v(58821.16, 55081.88) * mm, "end": v(60028.23, 54193.42) * mm});
            skLineSegment(sketch, "E1017", {"start": v(44184.43, 60123.13) * mm, "end": v(44567.28, 60238.99) * mm});
            skLineSegment(sketch, "E1018", {"start": v(44567.28, 60238.99) * mm, "end": v(44683.15, 59856.14) * mm});
            skLineSegment(sketch, "E1019", {"start": v(44683.15, 59856.14) * mm, "end": v(44300.3, 59740.27) * mm});
            skLineSegment(sketch, "E1020", {"start": v(44300.3, 59740.27) * mm, "end": v(44184.43, 60123.13) * mm});
            skLineSegment(sketch, "E1021", {"start": v(44567.28, 60238.99) * mm, "end": v(44300.3, 59740.27) * mm});
            skLineSegment(sketch, "E1022", {"start": v(44683.15, 59856.14) * mm, "end": v(44184.43, 60123.13) * mm});
            skLineSegment(sketch, "E1023", {"start": v(34476.97, 72521.3) * mm, "end": v(35369.84, 72634.42) * mm});
            skLineSegment(sketch, "E1024", {"start": v(35369.84, 72634.42) * mm, "end": v(35659.25, 70350.2) * mm});
            skLineSegment(sketch, "E1025", {"start": v(35659.25, 70350.2) * mm, "end": v(34766.39, 70237.07) * mm});
            skLineSegment(sketch, "E1026", {"start": v(34766.39, 70237.07) * mm, "end": v(34476.97, 72521.3) * mm});
            skLineSegment(sketch, "E1027", {"start": v(49850.78, 74290.55) * mm, "end": v(50844.73, 74417.28) * mm});
            skLineSegment(sketch, "E1028", {"start": v(50844.73, 74417.28) * mm, "end": v(51034.44, 72929.32) * mm});
            skLineSegment(sketch, "E1029", {"start": v(51034.44, 72929.32) * mm, "end": v(50040.49, 72802.6) * mm});
            skLineSegment(sketch, "E1030", {"start": v(50040.49, 72802.6) * mm, "end": v(49850.78, 74290.55) * mm});
            skLineSegment(sketch, "E1031", {"start": v(52423.14, 70002.5) * mm, "end": v(53813.88, 70179.82) * mm});
            skLineSegment(sketch, "E1032", {"start": v(53813.88, 70179.82) * mm, "end": v(54054.18, 68295.08) * mm});
            skLineSegment(sketch, "E1033", {"start": v(54054.18, 68295.08) * mm, "end": v(52663.44, 68117.76) * mm});
            skLineSegment(sketch, "E1034", {"start": v(52663.44, 68117.76) * mm, "end": v(52423.14, 70002.5) * mm});
            skLineSegment(sketch, "E1035", {"start": v(52646.83, 69829.4) * mm, "end": v(53640.78, 69956.14) * mm});
            skLineSegment(sketch, "E1036", {"start": v(53640.78, 69956.14) * mm, "end": v(53830.5, 68468.18) * mm});
            skLineSegment(sketch, "E1037", {"start": v(53830.5, 68468.18) * mm, "end": v(52836.54, 68341.45) * mm});
            skLineSegment(sketch, "E1038", {"start": v(52836.54, 68341.45) * mm, "end": v(52646.83, 69829.4) * mm});
            skLineSegment(sketch, "E1039", {"start": v(34700.56, 72348.02) * mm, "end": v(35196.66, 72410.88) * mm});
            skLineSegment(sketch, "E1040", {"start": v(35196.66, 72410.88) * mm, "end": v(35297.47, 71615.2) * mm});
            skLineSegment(sketch, "E1041", {"start": v(35297.47, 71615.2) * mm, "end": v(34801.37, 71552.35) * mm});
            skLineSegment(sketch, "E1042", {"start": v(34801.37, 71552.35) * mm, "end": v(34700.56, 72348.02) * mm});
            skLineSegment(sketch, "E1043", {"start": v(34839.58, 71254.46) * mm, "end": v(35336.24, 71317.88) * mm});
            skLineSegment(sketch, "E1044", {"start": v(35336.24, 71317.88) * mm, "end": v(35437.55, 70524.61) * mm});
            skLineSegment(sketch, "E1045", {"start": v(35437.55, 70524.61) * mm, "end": v(34940.89, 70461.18) * mm});
            skLineSegment(sketch, "E1046", {"start": v(34940.89, 70461.18) * mm, "end": v(34839.58, 71254.46) * mm});
            skLineSegment(sketch, "E1047", {"start": v(50844.73, 74417.28) * mm, "end": v(50040.49, 72802.6) * mm});
            skLineSegment(sketch, "E1048", {"start": v(34801.37, 71552.35) * mm, "end": v(35196.66, 72410.88) * mm});
            skLineSegment(sketch, "E1049", {"start": v(35297.47, 71615.2) * mm, "end": v(34700.56, 72348.02) * mm});
            skLineSegment(sketch, "E1050", {"start": v(34839.58, 71254.46) * mm, "end": v(35437.55, 70524.61) * mm});
            skLineSegment(sketch, "E1051", {"start": v(35336.24, 71317.88) * mm, "end": v(34940.89, 70461.18) * mm});
            skLineSegment(sketch, "E1052", {"start": v(49627.09, 74463.65) * mm, "end": v(51017.83, 74640.97) * mm});
            skLineSegment(sketch, "E1053", {"start": v(51017.83, 74640.97) * mm, "end": v(51258.13, 72756.22) * mm});
            skLineSegment(sketch, "E1054", {"start": v(51258.13, 72756.22) * mm, "end": v(49867.4, 72578.9) * mm});
            skLineSegment(sketch, "E1055", {"start": v(49867.4, 72578.9) * mm, "end": v(49627.09, 74463.65) * mm});
            skLineSegment(sketch, "E1056", {"start": v(38189.93, 60372.24) * mm, "end": v(38428.8, 60444.54) * mm});
            skLineSegment(sketch, "E1057", {"start": v(38428.8, 60444.54) * mm, "end": v(38501.23, 60205.27) * mm});
            skLineSegment(sketch, "E1058", {"start": v(38501.23, 60205.27) * mm, "end": v(38262.36, 60132.96) * mm});
            skLineSegment(sketch, "E1059", {"start": v(38262.36, 60132.96) * mm, "end": v(38189.93, 60372.24) * mm});
            skLineSegment(sketch, "E1060", {"start": v(59738.14, 53370.87) * mm, "end": v(59956.13, 53492.41) * mm});
            skLineSegment(sketch, "E1061", {"start": v(59956.13, 53492.41) * mm, "end": v(60077.88, 53274.06) * mm});
            skLineSegment(sketch, "E1062", {"start": v(60077.88, 53274.06) * mm, "end": v(59859.9, 53152.52) * mm});
            skLineSegment(sketch, "E1063", {"start": v(59859.9, 53152.52) * mm, "end": v(59738.14, 53370.87) * mm});
            skLineSegment(sketch, "E1064", {"start": v(55210.51, 59594.72) * mm, "end": v(55449.39, 59667.03) * mm});
            skLineSegment(sketch, "E1065", {"start": v(55449.39, 59667.03) * mm, "end": v(55521.81, 59427.75) * mm});
            skLineSegment(sketch, "E1066", {"start": v(55521.81, 59427.75) * mm, "end": v(55282.94, 59355.44) * mm});
            skLineSegment(sketch, "E1067", {"start": v(55282.94, 59355.44) * mm, "end": v(55210.51, 59594.72) * mm});
            skLineSegment(sketch, "E1068", {"start": v(55647.75, 58840.53) * mm, "end": v(55886.63, 58912.83) * mm});
            skLineSegment(sketch, "E1069", {"start": v(55886.63, 58912.83) * mm, "end": v(55959.05, 58673.55) * mm});
            skLineSegment(sketch, "E1070", {"start": v(55959.05, 58673.55) * mm, "end": v(55720.18, 58601.25) * mm});
            skLineSegment(sketch, "E1071", {"start": v(55720.18, 58601.25) * mm, "end": v(55647.75, 58840.53) * mm});
            skLineSegment(sketch, "E1072", {"start": v(37456.34, 66947.4) * mm, "end": v(37703.9, 66979.13) * mm});
            skLineSegment(sketch, "E1073", {"start": v(37703.9, 66979.13) * mm, "end": v(37735.69, 66731.16) * mm});
            skLineSegment(sketch, "E1074", {"start": v(37735.69, 66731.16) * mm, "end": v(37488.14, 66699.42) * mm});
            skLineSegment(sketch, "E1075", {"start": v(37488.14, 66699.42) * mm, "end": v(37456.34, 66947.4) * mm});
            skLineSegment(sketch, "E1076", {"start": v(47002.58, 67097.48) * mm, "end": v(47250.1, 67129.43) * mm});
            skLineSegment(sketch, "E1077", {"start": v(47250.1, 67129.43) * mm, "end": v(47282.11, 66881.48) * mm});
            skLineSegment(sketch, "E1078", {"start": v(47282.11, 66881.48) * mm, "end": v(47034.59, 66849.54) * mm});
            skLineSegment(sketch, "E1079", {"start": v(47034.59, 66849.54) * mm, "end": v(47002.58, 67097.48) * mm});
            skCircle(sketch, "E1080", {"center": v(59907.57, 53323.26) * mm, "radius": 100 * mm});
            skLineSegment(sketch, "E1081", {"start": v(54853.3, 52162.53) * mm, "end": v(55092.18, 52234.83) * mm});
            skLineSegment(sketch, "E1082", {"start": v(55092.18, 52234.83) * mm, "end": v(55164.6, 51995.55) * mm});
            skLineSegment(sketch, "E1083", {"start": v(55164.6, 51995.55) * mm, "end": v(54925.73, 51923.25) * mm});
            skLineSegment(sketch, "E1084", {"start": v(54925.73, 51923.25) * mm, "end": v(54853.3, 52162.53) * mm});
            skCircle(sketch, "E1085", {"center": v(61618.95, 49805.4) * mm, "radius": 100 * mm});
            skCircle(sketch, "E1086", {"center": v(66070.16, 51123.96) * mm, "radius": 100 * mm});
            skCircle(sketch, "E1087", {"center": v(64235.09, 54415.48) * mm, "radius": 100 * mm});
            skCircle(sketch, "E1088", {"center": v(55008.95, 52079.04) * mm, "radius": 100 * mm});
            skCircle(sketch, "E1089", {"center": v(55803.4, 58757.04) * mm, "radius": 100 * mm});
            skCircle(sketch, "E1090", {"center": v(55366.16, 59511.24) * mm, "radius": 100 * mm});
            skLineSegment(sketch, "E1091", {"start": v(54484.83, 61992.3) * mm, "end": v(54723.7, 62064.61) * mm});
            skLineSegment(sketch, "E1092", {"start": v(54723.7, 62064.61) * mm, "end": v(54796.13, 61825.33) * mm});
            skLineSegment(sketch, "E1093", {"start": v(54796.13, 61825.33) * mm, "end": v(54557.25, 61753.03) * mm});
            skLineSegment(sketch, "E1094", {"start": v(54557.25, 61753.03) * mm, "end": v(54484.83, 61992.3) * mm});
            skCircle(sketch, "E1095", {"center": v(54640.48, 61908.82) * mm, "radius": 100 * mm});
            skLineSegment(sketch, "E1096", {"start": v(54197.3, 62934.76) * mm, "end": v(54436.17, 63007.06) * mm});
            skLineSegment(sketch, "E1097", {"start": v(54436.17, 63007.06) * mm, "end": v(54508.6, 62767.78) * mm});
            skLineSegment(sketch, "E1098", {"start": v(54508.6, 62767.78) * mm, "end": v(54269.72, 62695.48) * mm});
            skLineSegment(sketch, "E1099", {"start": v(54269.72, 62695.48) * mm, "end": v(54197.3, 62934.76) * mm});
            skCircle(sketch, "E1100", {"center": v(54352.95, 62851.27) * mm, "radius": 100 * mm});
            skCircle(sketch, "E1101", {"center": v(53446.75, 65852.18) * mm, "radius": 100 * mm});
            skCircle(sketch, "E1102", {"center": v(52573.67, 67254.1) * mm, "radius": 100 * mm});
            skCircle(sketch, "E1103", {"center": v(47142.35, 66989.48) * mm, "radius": 100 * mm});
            skCircle(sketch, "E1104", {"center": v(37596.02, 66839.28) * mm, "radius": 100 * mm});
            skCircle(sketch, "E1105", {"center": v(33039.56, 65997.36) * mm, "radius": 100 * mm});
            skCircle(sketch, "E1106", {"center": v(34791.84, 60208.14) * mm, "radius": 100 * mm});
            skCircle(sketch, "E1107", {"center": v(36052.03, 56044.68) * mm, "radius": 100 * mm});
            skCircle(sketch, "E1108", {"center": v(38345.58, 60288.75) * mm, "radius": 100 * mm});
            skCircle(sketch, "E1109", {"center": v(43322.3, 61795.06) * mm, "radius": 100 * mm});
            skCircle(sketch, "E1110", {"center": v(46109.38, 61097.57) * mm, "radius": 100 * mm});
            skCircle(sketch, "E1111", {"center": v(48521.67, 61827.72) * mm, "radius": 100 * mm});
            skLineSegment(sketch, "E1112", {"start": v(50038.27, 60390.66) * mm, "end": v(50277.14, 60462.96) * mm});
            skLineSegment(sketch, "E1113", {"start": v(50277.14, 60462.96) * mm, "end": v(50349.57, 60223.68) * mm});
            skLineSegment(sketch, "E1114", {"start": v(50349.57, 60223.68) * mm, "end": v(50110.7, 60151.38) * mm});
            skLineSegment(sketch, "E1115", {"start": v(50110.7, 60151.38) * mm, "end": v(50038.27, 60390.66) * mm});
            skCircle(sketch, "E1116", {"center": v(50193.92, 60307.17) * mm, "radius": 100 * mm});
            skLineSegment(sketch, "E1117", {"start": v(60178.25, 61433.16) * mm, "end": v(60396.38, 61554.44) * mm});
            skLineSegment(sketch, "E1118", {"start": v(60396.38, 61554.44) * mm, "end": v(60517.86, 61335.93) * mm});
            skLineSegment(sketch, "E1119", {"start": v(60517.86, 61335.93) * mm, "end": v(60299.73, 61214.66) * mm});
            skLineSegment(sketch, "E1120", {"start": v(60299.73, 61214.66) * mm, "end": v(60178.25, 61433.16) * mm});
            skCircle(sketch, "E1121", {"center": v(60348, 61384.4) * mm, "radius": 100 * mm});
            skLineSegment(sketch, "E1122", {"start": v(57546.85, 54869.81) * mm, "end": v(57721.53, 54967.21) * mm});
            skLineSegment(sketch, "E1123", {"start": v(57721.53, 54967.21) * mm, "end": v(58208.52, 54093.8) * mm});
            skLineSegment(sketch, "E1124", {"start": v(58208.52, 54093.8) * mm, "end": v(58033.84, 53996.4) * mm});
            skLineSegment(sketch, "E1125", {"start": v(58033.84, 53996.4) * mm, "end": v(57546.85, 54869.81) * mm});
            skLineSegment(sketch, "E1126", {"start": v(56914.07, 56005.42) * mm, "end": v(57088.75, 56102.82) * mm});
            skLineSegment(sketch, "E1127", {"start": v(57088.75, 56102.82) * mm, "end": v(57283.55, 55753.45) * mm});
            skLineSegment(sketch, "E1128", {"start": v(57283.55, 55753.45) * mm, "end": v(57108.87, 55656.05) * mm});
            skLineSegment(sketch, "E1129", {"start": v(57108.87, 55656.05) * mm, "end": v(56914.07, 56005.42) * mm});
            skLineSegment(sketch, "E1130", {"start": v(49409.97, 64434.35) * mm, "end": v(49301.3, 64793.37) * mm});
            skLineSegment(sketch, "E1131", {"start": v(49301.3, 64793.37) * mm, "end": v(50067, 65025.12) * mm});
            skLineSegment(sketch, "E1132", {"start": v(50067, 65025.12) * mm, "end": v(50175.66, 64666.1) * mm});
            skLineSegment(sketch, "E1133", {"start": v(50175.66, 64666.1) * mm, "end": v(49409.97, 64434.35) * mm});
            skLineSegment(sketch, "E1134", {"start": v(34636.19, 60291.63) * mm, "end": v(34875.06, 60363.93) * mm});
            skLineSegment(sketch, "E1135", {"start": v(34875.06, 60363.93) * mm, "end": v(34947.49, 60124.65) * mm});
            skLineSegment(sketch, "E1136", {"start": v(34947.49, 60124.65) * mm, "end": v(34708.61, 60052.35) * mm});
            skLineSegment(sketch, "E1137", {"start": v(34708.61, 60052.35) * mm, "end": v(34636.19, 60291.63) * mm});
            skLineSegment(sketch, "E1138", {"start": v(35896.38, 56128.17) * mm, "end": v(36135.26, 56200.47) * mm});
            skLineSegment(sketch, "E1139", {"start": v(36135.26, 56200.47) * mm, "end": v(36207.68, 55961.2) * mm});
            skLineSegment(sketch, "E1140", {"start": v(36207.68, 55961.2) * mm, "end": v(35968.8, 55888.9) * mm});
            skLineSegment(sketch, "E1141", {"start": v(35968.8, 55888.9) * mm, "end": v(35896.38, 56128.17) * mm});
            skLineSegment(sketch, "E1142", {"start": v(36403, 64574.74) * mm, "end": v(36761.93, 64683.38) * mm});
            skLineSegment(sketch, "E1143", {"start": v(36761.93, 64683.38) * mm, "end": v(36993.68, 63917.69) * mm});
            skLineSegment(sketch, "E1144", {"start": v(36993.68, 63917.69) * mm, "end": v(36634.75, 63809.05) * mm});
            skLineSegment(sketch, "E1145", {"start": v(36634.75, 63809.05) * mm, "end": v(36403, 64574.74) * mm});
            skLineSegment(sketch, "E1146", {"start": v(33524.84, 66731.22) * mm, "end": v(33811.96, 66818.19) * mm});
            skLineSegment(sketch, "E1147", {"start": v(33811.96, 66818.19) * mm, "end": v(33920.67, 66459.29) * mm});
            skLineSegment(sketch, "E1148", {"start": v(33920.67, 66459.29) * mm, "end": v(33633.56, 66372.32) * mm});
            skLineSegment(sketch, "E1149", {"start": v(33633.56, 66372.32) * mm, "end": v(33524.84, 66731.22) * mm});
            skLineSegment(sketch, "E1150", {"start": v(40221.97, 65782.56) * mm, "end": v(40523.97, 65560.26) * mm});
            skLineSegment(sketch, "E1151", {"start": v(40523.97, 65560.26) * mm, "end": v(39931.17, 64754.91) * mm});
            skLineSegment(sketch, "E1152", {"start": v(39931.17, 64754.91) * mm, "end": v(39629.16, 64977.22) * mm});
            skLineSegment(sketch, "E1153", {"start": v(39629.16, 64977.22) * mm, "end": v(40221.97, 65782.56) * mm});
            skLineSegment(sketch, "E1154", {"start": v(47169.33, 67854.25) * mm, "end": v(47541.16, 67902.9) * mm});
            skLineSegment(sketch, "E1155", {"start": v(47541.16, 67902.9) * mm, "end": v(47644.93, 67109.65) * mm});
            skLineSegment(sketch, "E1156", {"start": v(47644.93, 67109.65) * mm, "end": v(47273.1, 67061) * mm});
            skLineSegment(sketch, "E1157", {"start": v(47273.1, 67061) * mm, "end": v(47169.33, 67854.25) * mm});
            skLineSegment(sketch, "E1158", {"start": v(36788.31, 55701.04) * mm, "end": v(36672.43, 56083.9) * mm});
            skLineSegment(sketch, "E1159", {"start": v(36672.43, 56083.9) * mm, "end": v(36816, 56127.34) * mm});
            skLineSegment(sketch, "E1160", {"start": v(36816, 56127.34) * mm, "end": v(36931.88, 55744.5) * mm});
            skLineSegment(sketch, "E1161", {"start": v(36931.88, 55744.5) * mm, "end": v(36788.31, 55701.04) * mm});
            skLineSegment(sketch, "E1162", {"start": v(54325.97, 61474.06) * mm, "end": v(54613.1, 61560.97) * mm});
            skLineSegment(sketch, "E1163", {"start": v(54613.1, 61560.97) * mm, "end": v(55047.66, 60125.3) * mm});
            skLineSegment(sketch, "E1164", {"start": v(55047.66, 60125.3) * mm, "end": v(54760.52, 60038.39) * mm});
            skLineSegment(sketch, "E1165", {"start": v(54760.52, 60038.39) * mm, "end": v(54325.97, 61474.06) * mm});
            skLineSegment(sketch, "E1166", {"start": v(41780.84, 66223.26) * mm, "end": v(42152.67, 66271.9) * mm});
            skLineSegment(sketch, "E1167", {"start": v(42152.67, 66271.9) * mm, "end": v(42256.44, 65478.66) * mm});
            skLineSegment(sketch, "E1168", {"start": v(42256.44, 65478.66) * mm, "end": v(41884.6, 65430.02) * mm});
            skLineSegment(sketch, "E1169", {"start": v(41884.6, 65430.02) * mm, "end": v(41780.84, 66223.26) * mm});
            skLineSegment(sketch, "E1170", {"start": v(37410.44, 55889.35) * mm, "end": v(37294.56, 56272.2) * mm});
            skLineSegment(sketch, "E1171", {"start": v(37294.56, 56272.2) * mm, "end": v(37438.13, 56315.65) * mm});
            skLineSegment(sketch, "E1172", {"start": v(37438.13, 56315.65) * mm, "end": v(37554, 55932.8) * mm});
            skLineSegment(sketch, "E1173", {"start": v(37554, 55932.8) * mm, "end": v(37410.44, 55889.35) * mm});
            skLineSegment(sketch, "E1174", {"start": v(38032.56, 56077.65) * mm, "end": v(37916.69, 56460.5) * mm});
            skLineSegment(sketch, "E1175", {"start": v(37916.69, 56460.5) * mm, "end": v(38155.97, 56532.92) * mm});
            skLineSegment(sketch, "E1176", {"start": v(38155.97, 56532.92) * mm, "end": v(38271.84, 56150.08) * mm});
            skLineSegment(sketch, "E1177", {"start": v(38271.84, 56150.08) * mm, "end": v(38032.56, 56077.65) * mm});
            skLineSegment(sketch, "E1178", {"start": v(55193.71, 59500.7) * mm, "end": v(54997.92, 59441.17) * mm});
            skLineSegment(sketch, "E1179", {"start": v(54997.92, 59441.17) * mm, "end": v(55097.59, 59262.42) * mm});
            skLineSegment(sketch, "E1180", {"start": v(55097.59, 59262.42) * mm, "end": v(55293.4, 59321.92) * mm});
            skLineSegment(sketch, "E1181", {"start": v(55293.4, 59321.92) * mm, "end": v(55193.71, 59500.7) * mm});
            skLineSegment(sketch, "E1182", {"start": v(44135.93, 60369.65) * mm, "end": v(43824.76, 60275.46) * mm});
            skLineSegment(sketch, "E1183", {"start": v(43824.76, 60275.46) * mm, "end": v(43535.06, 61232.58) * mm});
            skLineSegment(sketch, "E1184", {"start": v(43535.06, 61232.58) * mm, "end": v(43846.24, 61326.77) * mm});
            skLineSegment(sketch, "E1185", {"start": v(43846.24, 61326.77) * mm, "end": v(44135.93, 60369.65) * mm});
            skLineSegment(sketch, "E1186", {"start": v(45093.66, 60398.32) * mm, "end": v(44997.95, 60369.35) * mm});
            skLineSegment(sketch, "E1187", {"start": v(44997.95, 60369.35) * mm, "end": v(44925.53, 60608.63) * mm});
            skLineSegment(sketch, "E1188", {"start": v(44925.53, 60608.63) * mm, "end": v(45021.24, 60637.6) * mm});
            skLineSegment(sketch, "E1189", {"start": v(45021.24, 60637.6) * mm, "end": v(45093.66, 60398.32) * mm});
            skLineSegment(sketch, "E1190", {"start": v(57126.86, 66909.28) * mm, "end": v(57344.99, 67030.55) * mm});
            skLineSegment(sketch, "E1191", {"start": v(57344.99, 67030.55) * mm, "end": v(57466.47, 66812.05) * mm});
            skLineSegment(sketch, "E1192", {"start": v(57466.47, 66812.05) * mm, "end": v(57248.34, 66690.78) * mm});
            skLineSegment(sketch, "E1193", {"start": v(57248.34, 66690.78) * mm, "end": v(57126.86, 66909.28) * mm});
            skCircle(sketch, "E1194", {"center": v(57296.6, 66860.52) * mm, "radius": 100 * mm});
            skLineSegment(sketch, "E1195", {"start": v(48665.41, 64407.4) * mm, "end": v(50817.84, 65059.03) * mm});
            skLineSegment(sketch, "E1196", {"start": v(53236.72, 65072.83) * mm, "end": v(53523.86, 65159.74) * mm});
            skLineSegment(sketch, "E1197", {"start": v(53523.86, 65159.74) * mm, "end": v(54045.32, 63436.93) * mm});
            skLineSegment(sketch, "E1198", {"start": v(54045.32, 63436.93) * mm, "end": v(53758.18, 63350.02) * mm});
            skLineSegment(sketch, "E1199", {"start": v(53758.18, 63350.02) * mm, "end": v(53236.72, 65072.83) * mm});
            skLineSegment(sketch, "E1200", {"start": v(49601.8, 74661.76) * mm, "end": v(49677.77, 74066.6) * mm});
            skLineSegment(sketch, "E1201", {"start": v(49677.77, 74066.6) * mm, "end": v(49380.19, 74028.6) * mm});
            skLineSegment(sketch, "E1202", {"start": v(49380.19, 74028.6) * mm, "end": v(49304.21, 74623.77) * mm});
            skLineSegment(sketch, "E1203", {"start": v(60781.96, 51101.97) * mm, "end": v(61218.16, 51345.19) * mm});
            skLineSegment(sketch, "E1204", {"start": v(61218.16, 51345.19) * mm, "end": v(61461.66, 50908.48) * mm});
            skLineSegment(sketch, "E1205", {"start": v(61461.66, 50908.48) * mm, "end": v(61025.46, 50665.27) * mm});
            skLineSegment(sketch, "E1206", {"start": v(61025.46, 50665.27) * mm, "end": v(60781.96, 51101.97) * mm});
            skLineSegment(sketch, "E1207", {"start": v(56062.05, 59566.86) * mm, "end": v(56498.6, 59810.28) * mm});
            skLineSegment(sketch, "E1208", {"start": v(56498.6, 59810.28) * mm, "end": v(56742.1, 59373.58) * mm});
            skLineSegment(sketch, "E1209", {"start": v(56742.1, 59373.58) * mm, "end": v(56305.55, 59130.16) * mm});
            skLineSegment(sketch, "E1210", {"start": v(56305.55, 59130.16) * mm, "end": v(56062.05, 59566.86) * mm});
            skLineSegment(sketch, "E1211", {"start": v(58407.56, 55360.33) * mm, "end": v(58843.96, 55603.67) * mm});
            skLineSegment(sketch, "E1212", {"start": v(58843.96, 55603.67) * mm, "end": v(59087.46, 55166.97) * mm});
            skLineSegment(sketch, "E1213", {"start": v(59087.46, 55166.97) * mm, "end": v(58651.05, 54923.63) * mm});
            skLineSegment(sketch, "E1214", {"start": v(58651.05, 54923.63) * mm, "end": v(58407.56, 55360.33) * mm});
            skLineSegment(sketch, "E1215", {"start": v(50439.88, 69649.92) * mm, "end": v(50876.96, 69893.63) * mm});
            skLineSegment(sketch, "E1216", {"start": v(50876.96, 69893.63) * mm, "end": v(51120.46, 69456.93) * mm});
            skLineSegment(sketch, "E1217", {"start": v(51120.46, 69456.93) * mm, "end": v(50683.38, 69213.22) * mm});
            skLineSegment(sketch, "E1218", {"start": v(50683.38, 69213.22) * mm, "end": v(50439.88, 69649.92) * mm});
            skLineSegment(sketch, "E1219", {"start": v(53158.61, 64774.03) * mm, "end": v(53595.41, 65017.58) * mm});
            skLineSegment(sketch, "E1220", {"start": v(53595.41, 65017.58) * mm, "end": v(53838.91, 64580.88) * mm});
            skLineSegment(sketch, "E1221", {"start": v(53838.91, 64580.88) * mm, "end": v(53402.11, 64337.32) * mm});
            skLineSegment(sketch, "E1222", {"start": v(53402.11, 64337.32) * mm, "end": v(53158.61, 64774.03) * mm});
            skLineSegment(sketch, "E1223", {"start": v(49697.18, 72335.11) * mm, "end": v(49895.57, 72360.44) * mm});
            skLineSegment(sketch, "E1224", {"start": v(49895.57, 72360.44) * mm, "end": v(50013.33, 71437.92) * mm});
            skLineSegment(sketch, "E1225", {"start": v(50013.33, 71437.92) * mm, "end": v(49814.94, 71412.6) * mm});
            skLineSegment(sketch, "E1226", {"start": v(49814.94, 71412.6) * mm, "end": v(49697.18, 72335.11) * mm});
            skLineSegment(sketch, "E1227", {"start": v(53342.38, 67484.3) * mm, "end": v(54490.94, 68124.63) * mm});
            skLineSegment(sketch, "E1228", {"start": v(54490.94, 68124.63) * mm, "end": v(55131.28, 66976.06) * mm});
            skLineSegment(sketch, "E1229", {"start": v(55131.28, 66976.06) * mm, "end": v(53982.71, 66335.73) * mm});
            skLineSegment(sketch, "E1230", {"start": v(53982.71, 66335.73) * mm, "end": v(53342.38, 67484.3) * mm});
            skLineSegment(sketch, "E1231", {"start": v(59429.22, 56566.4) * mm, "end": v(60577.78, 57206.73) * mm});
            skLineSegment(sketch, "E1232", {"start": v(60577.78, 57206.73) * mm, "end": v(61218.11, 56058.17) * mm});
            skLineSegment(sketch, "E1233", {"start": v(61218.11, 56058.17) * mm, "end": v(60069.55, 55417.83) * mm});
            skLineSegment(sketch, "E1234", {"start": v(60069.55, 55417.83) * mm, "end": v(59429.22, 56566.4) * mm});
            skEllipse(sketch, "E1235", {"center": v(50534.92, 62319.96) * mm, "majorRadius": 158.75 * mm, "minorRadius": 158.75 * mm, "majorAxis": v(1, 0)});
            skArc(sketch, "E1236", {"start": v(50382.98, 62273.97) * mm, "mid": v(50460, 62180) * mm, "end": v(50580.9, 62168.02) * mm});
            skArc(sketch, "E1237", {"start": v(50686.86, 62365.95) * mm, "mid": v(50609.84, 62459.92) * mm, "end": v(50488.93, 62471.9) * mm});
            skLineSegment(sketch, "E1238", {"start": v(50580.9, 62168.02) * mm, "end": v(50488.93, 62471.9) * mm});
            skLineSegment(sketch, "E1239", {"start": v(50686.86, 62365.95) * mm, "end": v(50382.98, 62273.97) * mm});
            skLineSegment(sketch, "E1240", {"start": v(50488.93, 62471.9) * mm, "end": v(50146.36, 63603.7) * mm});
            skEllipse(sketch, "E1241", {"center": v(54694.5, 55886.04) * mm, "majorRadius": 158.75 * mm, "minorRadius": 158.75 * mm, "majorAxis": v(1, 0)});
            skArc(sketch, "E1242", {"start": v(54542.55, 55840.05) * mm, "mid": v(54619.57, 55746.08) * mm, "end": v(54740.48, 55734.1) * mm});
            skArc(sketch, "E1243", {"start": v(54846.43, 55932.03) * mm, "mid": v(54769.41, 56026) * mm, "end": v(54648.5, 56037.99) * mm});
            skLineSegment(sketch, "E1244", {"start": v(54740.48, 55734.1) * mm, "end": v(54648.5, 56037.99) * mm});
            skLineSegment(sketch, "E1245", {"start": v(54846.43, 55932.03) * mm, "end": v(54542.55, 55840.05) * mm});
            skLineSegment(sketch, "E1246", {"start": v(54648.5, 56037.99) * mm, "end": v(54305.93, 57169.78) * mm});
            skLineSegment(sketch, "E1247", {"start": v(53514.49, 50619.77) * mm, "end": v(53572.43, 50428.35) * mm});
            skLineSegment(sketch, "E1248", {"start": v(53572.43, 50428.35) * mm, "end": v(53457.57, 50393.59) * mm});
            skLineSegment(sketch, "E1249", {"start": v(53457.57, 50393.59) * mm, "end": v(53399.63, 50585.01) * mm});
            skLineSegment(sketch, "E1250", {"start": v(53399.63, 50585.01) * mm, "end": v(53514.49, 50619.77) * mm});
            skLineSegment(sketch, "E1251", {"start": v(53696.34, 50674.82) * mm, "end": v(53754.28, 50483.4) * mm});
            skLineSegment(sketch, "E1252", {"start": v(53754.28, 50483.4) * mm, "end": v(53639.42, 50448.63) * mm});
            skLineSegment(sketch, "E1253", {"start": v(53639.42, 50448.63) * mm, "end": v(53581.48, 50640.05) * mm});
            skLineSegment(sketch, "E1254", {"start": v(53581.48, 50640.05) * mm, "end": v(53696.34, 50674.82) * mm});
            skLineSegment(sketch, "E1255", {"start": v(53878.19, 50729.86) * mm, "end": v(53936.13, 50538.44) * mm});
            skLineSegment(sketch, "E1256", {"start": v(53936.13, 50538.44) * mm, "end": v(53821.28, 50503.67) * mm});
            skLineSegment(sketch, "E1257", {"start": v(53821.28, 50503.67) * mm, "end": v(53763.34, 50695.1) * mm});
            skLineSegment(sketch, "E1258", {"start": v(53763.34, 50695.1) * mm, "end": v(53878.19, 50729.86) * mm});
            skLineSegment(sketch, "E1259", {"start": v(68800.03, 49613.6) * mm, "end": v(52895.98, 44799.76) * mm});
            skLineSegment(sketch, "E1260", {"start": v(64824.99, 62739.91) * mm, "end": v(48922.75, 57926.63) * mm});
            skLineSegment(sketch, "E1261", {"start": v(63051.1, 64454.54) * mm, "end": v(48298.44, 59989.21) * mm});
            skLineSegment(sketch, "E1262", {"start": v(58279.05, 77095.62) * mm, "end": v(29227.41, 73368.86) * mm});
            skLineSegment(sketch, "E1263", {"start": v(50700.72, 66312.66) * mm, "end": v(57291.8, 44536.93) * mm});
            skLineSegment(sketch, "E1264", {"start": v(56137.88, 61183.94) * mm, "end": v(34457.3, 54621.67) * mm});
            skLineSegment(sketch, "E1265", {"start": v(53763.43, 65950.46) * mm, "end": v(32900.17, 59635.57) * mm});
            skLineSegment(sketch, "E1266", {"start": v(37800.23, 67883.79) * mm, "end": v(31024.37, 65832.87) * mm});
            skLineSegment(sketch, "E1267", {"start": v(61637.16, 69125.21) * mm, "end": v(32680.7, 60360.68) * mm});
            skLineSegment(sketch, "E1268", {"start": v(59917.1, 70856.14) * mm, "end": v(32056.39, 62423.27) * mm});
            skLineSegment(sketch, "E1269", {"start": v(58503.37, 75526.87) * mm, "end": v(30642.65, 67094) * mm});
            skLineSegment(sketch, "E1270", {"start": v(66863.03, 56006.6) * mm, "end": v(50960.79, 51193.3) * mm});
            skLineSegment(sketch, "E1271", {"start": v(67188.94, 54929.83) * mm, "end": v(51286.7, 50116.55) * mm});
            skLineSegment(sketch, "E1272", {"start": v(48161.86, 80551.5) * mm, "end": v(59147.71, 44256.2) * mm});
            skLineSegment(sketch, "E1273", {"start": v(46080.13, 79921.4) * mm, "end": v(50825.96, 64242) * mm});
            skLineSegment(sketch, "E1274", {"start": v(38710.33, 77690.7) * mm, "end": v(45197.28, 56258.97) * mm});
            skLineSegment(sketch, "E1275", {"start": v(32335.92, 75761.3) * mm, "end": v(38822.87, 54329.57) * mm});
            skLineSegment(sketch, "E1276", {"start": v(29943.13, 75037.05) * mm, "end": v(36430.08, 53605.32) * mm});
            skLineSegment(sketch, "E1277", {"start": v(67769.85, 47708.43) * mm, "end": v(50010.94, 79562.53) * mm});
            skCircle(sketch, "E1278", {"center": v(29827.25, 75419.9) * mm, "radius": 400 * mm});
            skCircle(sketch, "E1279", {"center": v(32220.04, 76144.15) * mm, "radius": 400 * mm});
            skCircle(sketch, "E1280", {"center": v(38594.44, 78073.55) * mm, "radius": 400 * mm});
            skCircle(sketch, "E1281", {"center": v(45967.29, 80305.16) * mm, "radius": 400 * mm});
            skCircle(sketch, "E1282", {"center": v(48042.95, 80933.4) * mm, "radius": 400 * mm});
            skCircle(sketch, "E1283", {"center": v(58675.8, 77146.49) * mm, "radius": 400 * mm});
            skCircle(sketch, "E1284", {"center": v(51669.85, 81022.14) * mm, "radius": 400 * mm});
            skCircle(sketch, "E1285", {"center": v(55953.69, 77875.9) * mm, "radius": 400 * mm});
            skCircle(sketch, "E1286", {"center": v(58886.21, 75642.75) * mm, "radius": 400 * mm});
            skCircle(sketch, "E1287", {"center": v(60299.95, 70972.02) * mm, "radius": 400 * mm});
            skCircle(sketch, "E1288", {"center": v(62020, 69241.1) * mm, "radius": 400 * mm});
            skCircle(sketch, "E1289", {"center": v(63433.94, 64570.42) * mm, "radius": 400 * mm});
            skCircle(sketch, "E1290", {"center": v(65207.84, 62855.8) * mm, "radius": 400 * mm});
            skCircle(sketch, "E1291", {"center": v(66621.57, 58185.06) * mm, "radius": 400 * mm});
            skCircle(sketch, "E1292", {"center": v(67245.88, 56122.47) * mm, "radius": 400 * mm});
            skCircle(sketch, "E1293", {"center": v(69182.88, 49729.47) * mm, "radius": 400 * mm});
            skCircle(sketch, "E1294", {"center": v(28686.24, 72177.64) * mm, "radius": 400 * mm});
            skCircle(sketch, "E1295", {"center": v(30641.28, 65716.92) * mm, "radius": 400 * mm});
            skCircle(sketch, "E1296", {"center": v(32515.18, 59519.04) * mm, "radius": 400 * mm});
            skCircle(sketch, "E1297", {"center": v(34071.81, 54504.99) * mm, "radius": 400 * mm});
            skCircle(sketch, "E1298", {"center": v(48987.18, 56326.68) * mm, "radius": 400 * mm});
            skCircle(sketch, "E1299", {"center": v(49399.16, 79054.72) * mm, "radius": 400 * mm});
            skLineSegment(sketch, "E1300", {"start": v(36305.06, 74483.7) * mm, "end": v(29069.58, 72293.67) * mm});
            skLineSegment(sketch, "E1301", {"start": v(66238.73, 58069.18) * mm, "end": v(50336.48, 53255.9) * mm});
            skLineSegment(sketch, "E1302", {"start": v(53375.44, 75865.5) * mm, "end": v(51312.22, 74715.25) * mm});
            skLineSegment(sketch, "E1303", {"start": v(51499.4, 78348.17) * mm, "end": v(51983.24, 74576.36) * mm});
            skLineSegment(sketch, "E1304", {"start": v(35636.54, 59235.4) * mm, "end": v(51432.72, 80700.01) * mm});
            skLineSegment(sketch, "E1305", {"start": v(39916.94, 56084.63) * mm, "end": v(55716.5, 77553.82) * mm});
            skCircle(sketch, "E1306", {"center": v(67571.79, 55045.71) * mm, "radius": 400 * mm});
            skCircle(sketch, "E1307", {"center": v(65653.83, 61371.34) * mm, "radius": 400 * mm});
            skCircle(sketch, "E1308", {"center": v(63682.27, 63752.25) * mm, "radius": 400 * mm});
            skLineSegment(sketch, "E1309", {"start": v(65270.99, 61255.46) * mm, "end": v(49371.78, 56443.1) * mm});
            skCircle(sketch, "E1310", {"center": v(57407.68, 44154.09) * mm, "radius": 400 * mm});
            skCircle(sketch, "E1311", {"center": v(54584.18, 43299.47) * mm, "radius": 400 * mm});
            skCircle(sketch, "E1312", {"center": v(67964.63, 47359.05) * mm, "radius": 400 * mm});
            skLineSegment(sketch, "E1313", {"start": v(54468.58, 43682.4) * mm, "end": v(49533.34, 59987.56) * mm});
            skLineSegment(sketch, "E1314", {"start": v(67004.16, 47476.67) * mm, "end": v(49593.94, 78705.35) * mm});
            skCircle(sketch, "E1315", {"center": v(49816.16, 79911.9) * mm, "radius": 400 * mm});
            skCircle(sketch, "E1316", {"center": v(67198.94, 47127.3) * mm, "radius": 400 * mm});
            skLineSegment(sketch, "E1317", {"start": v(63299.42, 63636.4) * mm, "end": v(48546.14, 59170.88) * mm});
            skSolve(sketch);
        }
        {
            var Q0;
            Q0=qCreatedBy(makeId("Top.planeOp"),FACE);
            var sketch = newSketch(context, id + "F2", { "sketchPlane" : qUnion([Q0])});
            skLineSegment(sketch, "E1318.0", {"start": v(54145.32, 46326.6) * mm, "end": v(52902.06, 50434.12) * mm});
            skLineSegment(sketch, "E1318.1", {"start": v(67150.92, 50263.13) * mm, "end": v(54431.42, 46413.2) * mm});
            skLineSegment(sketch, "E1318.2", {"start": v(67150.92, 50263.13) * mm, "end": v(54145.32, 46326.6) * mm});
            skLineSegment(sketch, "E1318.3", {"start": v(53909.98, 50739.2) * mm, "end": v(57604, 51858.9) * mm});
            skLineSegment(sketch, "E1318.4", {"start": v(53075.2, 75510.7) * mm, "end": v(67150.92, 50263.13) * mm});
            skLineSegment(sketch, "E1318.5", {"start": v(54874.02, 59663.37) * mm, "end": v(58991.9, 52278.2) * mm});
            skLineSegment(sketch, "E1318.6", {"start": v(54760.52, 60038.39) * mm, "end": v(54325.97, 61474.06) * mm});
            skLineSegment(sketch, "E1318.7", {"start": v(53225.02, 65066.3) * mm, "end": v(53000.6, 65468.81) * mm});
            skLineSegment(sketch, "E1318.9", {"start": v(49304.21, 74623.77) * mm, "end": v(49909.66, 69880.9) * mm});
            skLineSegment(sketch, "E1318.10", {"start": v(49253.57, 75020.46) * mm, "end": v(53075.2, 75510.7) * mm});
            skLineSegment(sketch, "E1319", {"start": v(50281.68, 69933.64) * mm, "end": v(49909.66, 69880.9) * mm});
            skLineSegment(sketch, "E1320", {"start": v(54325.97, 61474.06) * mm, "end": v(53225.02, 65066.3) * mm});
            skLineSegment(sketch, "E1321", {"start": v(53000.6, 65468.81) * mm, "end": v(50281.68, 69933.64) * mm});
            skLineSegment(sketch, "E1322", {"start": v(54874.02, 59663.37) * mm, "end": v(54760.52, 60038.39) * mm});
            skLineSegment(sketch, "E1323", {"start": v(49304.21, 74623.77) * mm, "end": v(49253.57, 75020.46) * mm});
            skLineSegment(sketch, "E1324", {"start": v(53909.98, 50739.2) * mm, "end": v(52902.06, 50434.12) * mm});
            skLineSegment(sketch, "E1325", {"start": v(58991.9, 52278.2) * mm, "end": v(57604, 51858.9) * mm});
            skLineSegment(sketch, "E1326", {"start": v(53342.81, 50358.57) * mm, "end": v(59287.5, 52158.7) * mm});
            skLineSegment(sketch, "E1327", {"start": v(54412.26, 46825.31) * mm, "end": v(53342.81, 50358.57) * mm});
            skLineSegment(sketch, "E1328", {"start": v(54412.26, 46825.31) * mm, "end": v(66559.72, 50502.1) * mm});
            skLineSegment(sketch, "E1329", {"start": v(52857.63, 75079.51) * mm, "end": v(66559.72, 50502.1) * mm});
            skLineSegment(sketch, "E1330", {"start": v(49601.8, 74661.76) * mm, "end": v(52857.63, 75079.51) * mm});
            skLineSegment(sketch, "E1331", {"start": v(50131.26, 70514.15) * mm, "end": v(49601.8, 74661.76) * mm});
            skLineSegment(sketch, "E1332", {"start": v(50504.39, 70561.9) * mm, "end": v(50131.26, 70514.15) * mm});
            skLineSegment(sketch, "E1333", {"start": v(50504.39, 70561.9) * mm, "end": v(53523.86, 65159.74) * mm});
            skLineSegment(sketch, "E1334", {"start": v(55070.83, 59721.1) * mm, "end": v(53523.86, 65159.74) * mm});
            skLineSegment(sketch, "E1335", {"start": v(59287.5, 52158.7) * mm, "end": v(55070.83, 59721.1) * mm});
            skSolve(sketch);
        }
        {
            var Q0;
            Q0=qSketchRegion(id+"F2",true);
            extrude(context, id + "F3", {"entities" : qUnion([Q0]), "depth" : (getVariable(context, 'Ceiling')) * mm, "offsetDistance" : 25 * mm});
        }
        {
            var Q0;
            Q0=qCreatedBy(makeId("Top.planeOp"),FACE);
            var sketch = newSketch(context, id + "F4", { "sketchPlane" : qUnion([Q0])});
            skLineSegment(sketch, "E1336.0", {"start": v(54874.02, 59663.37) * mm, "end": v(58991.9, 52278.2) * mm});
            skLineSegment(sketch, "E1336.1", {"start": v(58991.9, 52278.2) * mm, "end": v(57604, 51858.9) * mm});
            skLineSegment(sketch, "E1336.2", {"start": v(53909.98, 50739.2) * mm, "end": v(57604, 51858.9) * mm});
            skLineSegment(sketch, "E1336.3", {"start": v(53909.98, 50739.2) * mm, "end": v(52902.06, 50434.12) * mm});
            skLineSegment(sketch, "E1336.4", {"start": v(54145.32, 46326.6) * mm, "end": v(52902.06, 50434.12) * mm});
            skLineSegment(sketch, "E1336.5", {"start": v(67150.92, 50263.13) * mm, "end": v(54145.32, 46326.6) * mm});
            skLineSegment(sketch, "E1336.6", {"start": v(53075.2, 75510.7) * mm, "end": v(67150.92, 50263.13) * mm});
            skLineSegment(sketch, "E1337.0", {"start": v(54874.02, 59663.37) * mm, "end": v(54760.52, 60038.39) * mm});
            skLineSegment(sketch, "E1337.1", {"start": v(54760.52, 60038.39) * mm, "end": v(54325.97, 61474.06) * mm});
            skLineSegment(sketch, "E1337.2", {"start": v(54325.97, 61474.06) * mm, "end": v(53225.02, 65066.3) * mm});
            skLineSegment(sketch, "E1337.3", {"start": v(53000.6, 65468.81) * mm, "end": v(50281.68, 69933.64) * mm});
            skLineSegment(sketch, "E1337.4", {"start": v(53225.02, 65066.3) * mm, "end": v(53000.6, 65468.81) * mm});
            skLineSegment(sketch, "E1337.5", {"start": v(50281.68, 69933.64) * mm, "end": v(49909.66, 69880.9) * mm});
            skLineSegment(sketch, "E1337.6", {"start": v(49304.21, 74623.77) * mm, "end": v(49909.66, 69880.9) * mm});
            skLineSegment(sketch, "E1337.7", {"start": v(49304.21, 74623.77) * mm, "end": v(49253.57, 75020.46) * mm});
            skLineSegment(sketch, "E1337.8", {"start": v(49253.57, 75020.46) * mm, "end": v(53075.2, 75510.7) * mm});
            skSolve(sketch);
        }
        {
            var Q0;
            Q0=qSketchRegion(id+"F4",true);
            extrude(context, id + "F5", {"entities" : qUnion([Q0]), "oppositeDirection" : true, "depth" : 25 * mm, "offsetDistance" : 25 * mm});
        }
        {
            var Q0;
            Q0=qCreatedBy(makeId("Top.planeOp"),FACE);
            var sketch = newSketch(context, id + "F6", { "sketchPlane" : qUnion([Q0])});
            skLineSegment(sketch, "E1338.0", {"start": v(62899.33, 55116.74) * mm, "end": v(63167.18, 54636.37) * mm});
            skLineSegment(sketch, "E1338.1", {"start": v(62948.82, 54514.62) * mm, "end": v(63167.18, 54636.37) * mm});
            skLineSegment(sketch, "E1338.2", {"start": v(62680.98, 54995) * mm, "end": v(62948.82, 54514.62) * mm});
            skLineSegment(sketch, "E1338.3", {"start": v(62680.98, 54995) * mm, "end": v(62899.33, 55116.74) * mm});
            skLineSegment(sketch, "E1338.4", {"start": v(61874.42, 56441.78) * mm, "end": v(62092.77, 56563.53) * mm});
            skLineSegment(sketch, "E1338.5", {"start": v(61606.57, 56922.15) * mm, "end": v(61824.92, 57043.9) * mm});
            skLineSegment(sketch, "E1338.6", {"start": v(61824.92, 57043.9) * mm, "end": v(62092.77, 56563.53) * mm});
            skLineSegment(sketch, "E1338.7", {"start": v(61606.57, 56922.15) * mm, "end": v(61874.42, 56441.78) * mm});
            skPoint(sketch, "E1338.8", {"position": v(61983.6, 56502.65) * mm});
            skLineSegment(sketch, "E1339.0", {"start": v(59826.06, 53123.27) * mm, "end": v(60131.76, 53293.71) * mm});
            skLineSegment(sketch, "E1339.1", {"start": v(60131.76, 53293.71) * mm, "end": v(60570.05, 52507.65) * mm});
            skLineSegment(sketch, "E1339.2", {"start": v(60264.36, 52337.2) * mm, "end": v(60570.05, 52507.65) * mm});
            skLineSegment(sketch, "E1339.3", {"start": v(59826.06, 53123.27) * mm, "end": v(60264.36, 52337.2) * mm});
            skLineSegment(sketch, "E1340.0", {"start": v(56060.35, 60596.37) * mm, "end": v(56498.65, 59810.3) * mm});
            skPoint(sketch, "E1340.1", {"position": v(56060.35, 60596.37) * mm});
            skLineSegment(sketch, "E1340.2", {"start": v(55754.66, 60425.92) * mm, "end": v(56060.35, 60596.37) * mm});
            skLineSegment(sketch, "E1340.3", {"start": v(55754.66, 60425.92) * mm, "end": v(56192.96, 59639.86) * mm});
            skLineSegment(sketch, "E1340.4", {"start": v(56192.96, 59639.86) * mm, "end": v(56498.65, 59810.3) * mm});
            skLineSegment(sketch, "E1340.5", {"start": v(59174.97, 61283.7) * mm, "end": v(59393.32, 61405.46) * mm});
            skLineSegment(sketch, "E1340.6", {"start": v(59442.82, 60803.34) * mm, "end": v(59661.17, 60925.09) * mm});
            skLineSegment(sketch, "E1340.7", {"start": v(59174.97, 61283.7) * mm, "end": v(59442.82, 60803.34) * mm});
            skLineSegment(sketch, "E1340.8", {"start": v(59393.32, 61405.46) * mm, "end": v(59661.17, 60925.09) * mm});
            skLineSegment(sketch, "E1340.9", {"start": v(58318.92, 63332.61) * mm, "end": v(58586.76, 62852.24) * mm});
            skLineSegment(sketch, "E1340.10", {"start": v(58100.57, 63210.86) * mm, "end": v(58318.92, 63332.61) * mm});
            skLineSegment(sketch, "E1340.11", {"start": v(58100.57, 63210.86) * mm, "end": v(58368.41, 62730.5) * mm});
            skLineSegment(sketch, "E1340.12", {"start": v(58368.41, 62730.5) * mm, "end": v(58586.76, 62852.24) * mm});
            skPoint(sketch, "E1340.13", {"position": v(56279.5, 60203.34) * mm});
            skPoint(sketch, "E1340.14", {"position": v(59527.24, 61165.27) * mm});
            skSolve(sketch);
        }
        {
            var Q0;
            Q0=qSketchRegion(id+"F6",true);
            extrude(context, id + "F7", {"entities" : qUnion([Q0]), "operationType" : NewBodyOperationType.ADD, "depth" : (getVariable(context, 'Ceiling')) * mm, "offsetDistance" : 25 * mm});
        }
        {
            var Q0;
            Q0=qCreatedBy(makeId("Top.planeOp"),FACE);
            var sketch = newSketch(context, id + "F8", { "sketchPlane" : qUnion([Q0])});
            skLineSegment(sketch, "E1341.0", {"start": v(64867.16, 51074.04) * mm, "end": v(51575.28, 74914.98) * mm, "construction": true});
            skPoint(sketch, "E1342.0", {"position": v(56060.35, 60596.37) * mm});
            skLineSegment(sketch, "E1343", {"start": v(56060.35, 60596.37) * mm, "end": v(58728.8, 62084.09) * mm});
            skLineSegment(sketch, "E1344.0", {"start": v(61899.36, 49097.97) * mm, "end": v(50281.68, 69933.64) * mm, "construction": true});
            skLineSegment(sketch, "E1345", {"start": v(58565.38, 55077.28) * mm, "end": v(61670.18, 56808.28) * mm});
            skLineSegment(sketch, "E1346", {"start": v(61670.18, 56808.28) * mm, "end": v(58728.8, 62084.09) * mm});
            skLineSegment(sketch, "E1347.0", {"start": v(55070.83, 59721.1) * mm, "end": v(53523.86, 65159.74) * mm, "construction": true});
            skLineSegment(sketch, "E1347.1", {"start": v(55070.83, 59721.1) * mm, "end": v(59287.5, 52158.7) * mm, "construction": true});
            skLineSegment(sketch, "E1348", {"start": v(55754.66, 60425.92) * mm, "end": v(54991.4, 60000.34) * mm});
            skLineSegment(sketch, "E1349", {"start": v(54991.4, 60000.34) * mm, "end": v(55070.83, 59721.1) * mm});
            skLineSegment(sketch, "E1350", {"start": v(58565.38, 55077.28) * mm, "end": v(57874.84, 54692.24) * mm});
            skLineSegment(sketch, "E1351", {"start": v(57874.84, 54692.24) * mm, "end": v(55102.82, 59663.72) * mm});
            skLineSegment(sketch, "E1352", {"start": v(55102.82, 59663.72) * mm, "end": v(55070.83, 59721.1) * mm});
            skLineSegment(sketch, "E1353.0", {"start": v(55754.66, 60425.92) * mm, "end": v(56192.96, 59639.86) * mm});
            skLineSegment(sketch, "E1353.1", {"start": v(56192.96, 59639.86) * mm, "end": v(56498.65, 59810.3) * mm});
            skLineSegment(sketch, "E1353.2", {"start": v(56060.35, 60596.37) * mm, "end": v(56498.65, 59810.3) * mm});
            skSolve(sketch);
        }
        {
            var Q0;
            Q0=qSketchRegion(id+"F8",true);
            extrude(context, id + "F9", {"entities" : qUnion([Q0]), "depth" : 150 * mm, "offsetDistance" : 25 * mm});
        }
        {
            var Q0;
            Q0=makeQuery(id+"F5.opExtrude","CAP_FACE",FACE,{"disambiguationData":[OSD([sQuery(id+"F4.wireOp",EDGE,"E1336.0"),sQuery(id+"F4.wireOp",EDGE,"E1336.1"),sQuery(id+"F4.wireOp",EDGE,"E1336.2"),sQuery(id+"F4.wireOp",EDGE,"E1336.3"),sQuery(id+"F4.wireOp",EDGE,"E1336.4"),sQuery(id+"F4.wireOp",EDGE,"E1336.5"),sQuery(id+"F4.wireOp",EDGE,"E1336.6"),sQuery(id+"F4.wireOp",EDGE,"E1337.0"),sQuery(id+"F4.wireOp",EDGE,"E1337.1"),sQuery(id+"F4.wireOp",EDGE,"E1337.2"),sQuery(id+"F4.wireOp",EDGE,"E1337.3"),sQuery(id+"F4.wireOp",EDGE,"E1337.4"),sQuery(id+"F4.wireOp",EDGE,"E1337.5"),sQuery(id+"F4.wireOp",EDGE,"E1337.6"),sQuery(id+"F4.wireOp",EDGE,"E1337.7"),sQuery(id+"F4.wireOp",EDGE,"E1337.8")])],"isStart":true});
            var sketch = newSketch(context, id + "F10", { "sketchPlane" : qUnion([Q0])});
            skLineSegment(sketch, "E1354.0", {"start": v(60028.23, 54193.42) * mm, "end": v(59168.74, 53933.32) * mm});
            skLineSegment(sketch, "E1354.1", {"start": v(59168.74, 53933.32) * mm, "end": v(58821.16, 55081.88) * mm});
            skLineSegment(sketch, "E1354.2", {"start": v(58821.16, 55081.88) * mm, "end": v(59680.65, 55341.98) * mm});
            skLineSegment(sketch, "E1354.3", {"start": v(59680.65, 55341.98) * mm, "end": v(60028.23, 54193.42) * mm});
            skSolve(sketch);
        }
        {
            var Q0;
            Q0=qSketchRegion(id+"F10",true);
            extrude(context, id + "F11", {"entities" : qUnion([Q0]), "operationType" : NewBodyOperationType.REMOVE, "endBound" : BoundingType.THROUGH_ALL, "oppositeDirection" : true, "depth" : 25 * mm, "offsetDistance" : 25 * mm});
        }
    });
